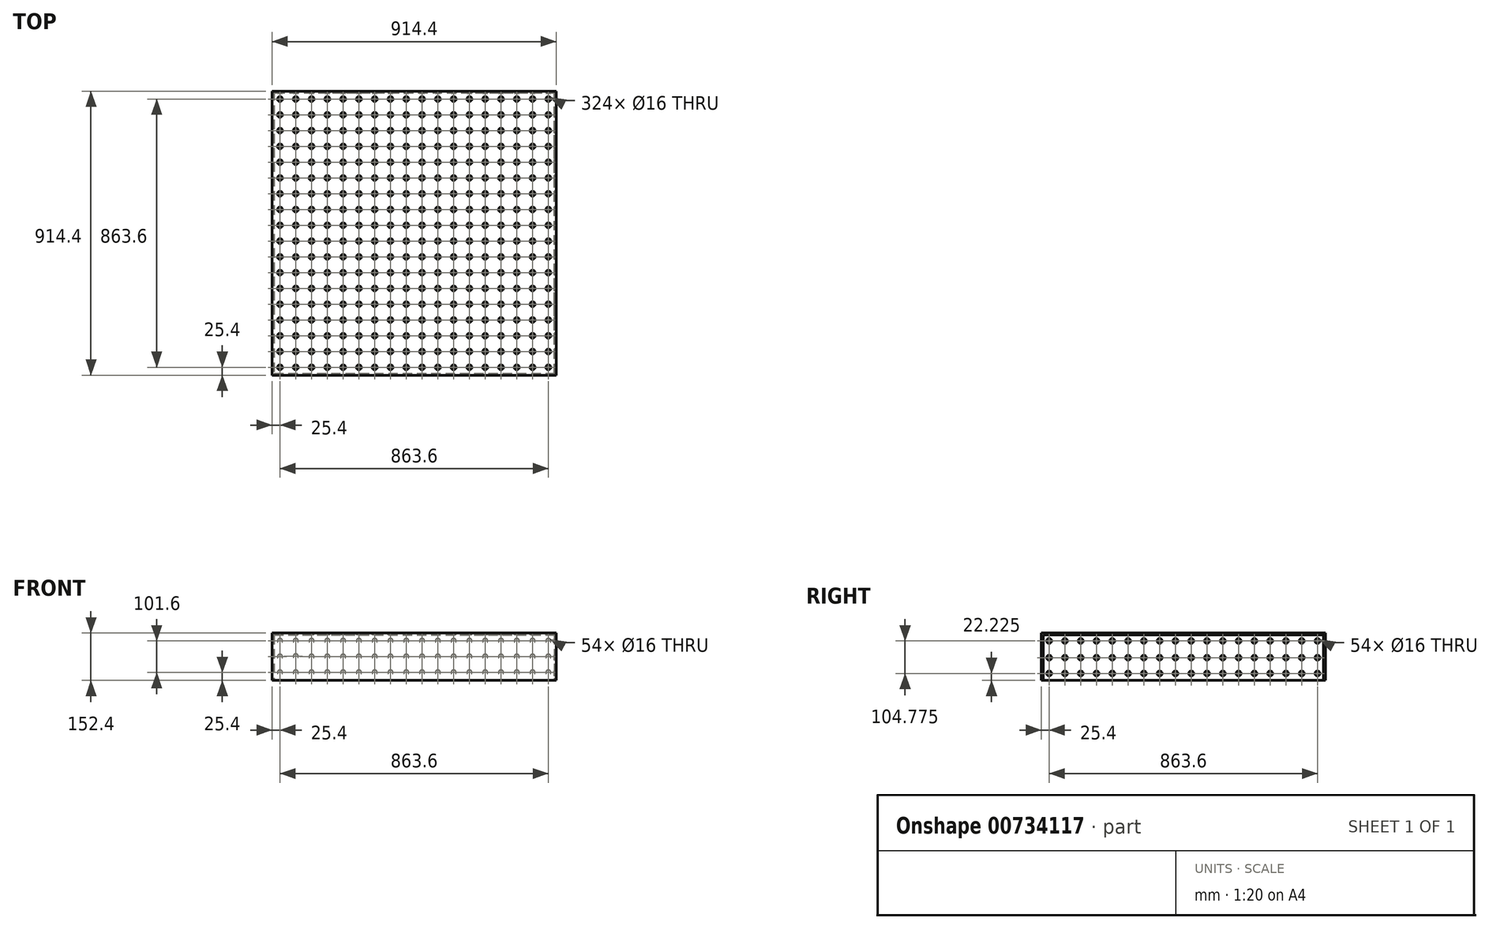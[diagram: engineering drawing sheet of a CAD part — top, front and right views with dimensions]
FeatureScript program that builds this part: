
annotation { "Feature Type Name" : "Feature", "Feature Type Description" : "" }
export const myFeature = defineFeature(function(context is Context, id is Id, definition is map)
    precondition{}
    {
        {
            var Q0;
            Q0=qCreatedBy(makeId("Top.planeOp"),FACE);
            var sketch = newSketch(context, id + "F0", { "sketchPlane" : qUnion([Q0])});
            skLineSegment(sketch, "E0.bottom", {"start": v(-457.2, 457.2) * mm, "end": v(457.2, 457.2) * mm});
            skLineSegment(sketch, "E0.top", {"start": v(-457.2, -457.2) * mm, "end": v(457.2, -457.2) * mm});
            skLineSegment(sketch, "E0.left", {"start": v(-457.2, 457.2) * mm, "end": v(-457.2, -457.2) * mm});
            skLineSegment(sketch, "E0.right", {"start": v(457.2, 457.2) * mm, "end": v(457.2, -457.2) * mm});
            skPoint(sketch, "E0.middle", {"position": v(0, 0) * mm});
            skSolve(sketch);
        }
        {
            var Q0;
            Q0 = qSketchRegion(id + "F0", true);
            extrude(context, id + "F1", {"entities" : qUnion([Q0]), "depth" : 6.35 * mm, "offsetDistance" : 25.4 * mm});
        }
        {
            var Q0;
            Q0=makeQuery(id+"F1.opExtrude","CAP_FACE",FACE,{"disambiguationData":[OSD([sQuery(id+"F0.wireOp",EDGE,"E0.bottom"),sQuery(id+"F0.wireOp",EDGE,"E0.top"),sQuery(id+"F0.wireOp",EDGE,"E0.left"),sQuery(id+"F0.wireOp",EDGE,"E0.right")])],"isStart":false});
            var sketch = newSketch(context, id + "F2", { "sketchPlane" : qUnion([Q0])});
            skLineSegment(sketch, "E1", {"start": v(-431.8, 457.2) * mm, "end": v(-431.8, -457.2) * mm, "construction": true});
            skLineSegment(sketch, "E2", {"start": v(-381, 457.2) * mm, "end": v(-381, -457.2) * mm, "construction": true});
            skLineSegment(sketch, "E3", {"start": v(-330.2, 457.2) * mm, "end": v(-330.2, -457.2) * mm, "construction": true});
            skLineSegment(sketch, "E4", {"start": v(-279.4, 457.2) * mm, "end": v(-279.4, -457.2) * mm, "construction": true});
            skLineSegment(sketch, "E5", {"start": v(-228.6, 457.2) * mm, "end": v(-228.6, -457.2) * mm, "construction": true});
            skLineSegment(sketch, "E6", {"start": v(-177.8, 457.2) * mm, "end": v(-177.8, -457.2) * mm, "construction": true});
            skLineSegment(sketch, "E7", {"start": v(-127, 457.2) * mm, "end": v(-127, -457.2) * mm, "construction": true});
            skLineSegment(sketch, "E8", {"start": v(-76.2, 457.2) * mm, "end": v(-76.2, -457.2) * mm, "construction": true});
            skLineSegment(sketch, "E9", {"start": v(-25.4, 457.2) * mm, "end": v(-25.4, -457.2) * mm, "construction": true});
            skLineSegment(sketch, "E10", {"start": v(25.4, 457.2) * mm, "end": v(25.4, -457.2) * mm, "construction": true});
            skLineSegment(sketch, "E11", {"start": v(76.2, 457.2) * mm, "end": v(76.2, -457.2) * mm, "construction": true});
            skLineSegment(sketch, "E12", {"start": v(127, 457.2) * mm, "end": v(127, -457.2) * mm, "construction": true});
            skLineSegment(sketch, "E13", {"start": v(177.8, 457.2) * mm, "end": v(177.8, -457.2) * mm, "construction": true});
            skLineSegment(sketch, "E14", {"start": v(228.6, 457.2) * mm, "end": v(228.6, -457.2) * mm, "construction": true});
            skLineSegment(sketch, "E15", {"start": v(279.4, 457.2) * mm, "end": v(279.4, -457.2) * mm, "construction": true});
            skLineSegment(sketch, "E16", {"start": v(330.2, 457.2) * mm, "end": v(330.2, -457.2) * mm, "construction": true});
            skLineSegment(sketch, "E17", {"start": v(381, 457.2) * mm, "end": v(381, -457.2) * mm, "construction": true});
            skLineSegment(sketch, "E18", {"start": v(431.8, 457.2) * mm, "end": v(431.8, -457.2) * mm, "construction": true});
            skLineSegment(sketch, "E19", {"start": v(-457.2, 431.8) * mm, "end": v(457.2, 431.8) * mm, "construction": true});
            skLineSegment(sketch, "E20", {"start": v(-457.2, 381) * mm, "end": v(457.2, 381) * mm, "construction": true});
            skLineSegment(sketch, "E21", {"start": v(-457.2, 330.2) * mm, "end": v(457.2, 330.2) * mm, "construction": true});
            skLineSegment(sketch, "E22", {"start": v(-457.2, 279.4) * mm, "end": v(457.2, 279.4) * mm, "construction": true});
            skLineSegment(sketch, "E23", {"start": v(-457.2, 228.6) * mm, "end": v(457.2, 228.6) * mm, "construction": true});
            skLineSegment(sketch, "E24", {"start": v(-457.2, 177.8) * mm, "end": v(457.2, 177.8) * mm, "construction": true});
            skLineSegment(sketch, "E25", {"start": v(-457.2, 127) * mm, "end": v(457.2, 127) * mm, "construction": true});
            skLineSegment(sketch, "E26", {"start": v(-457.2, 76.2) * mm, "end": v(457.2, 76.2) * mm, "construction": true});
            skLineSegment(sketch, "E27", {"start": v(-457.2, 25.4) * mm, "end": v(457.2, 25.4) * mm, "construction": true});
            skLineSegment(sketch, "E28", {"start": v(-457.2, -25.4) * mm, "end": v(457.2, -25.4) * mm, "construction": true});
            skLineSegment(sketch, "E29", {"start": v(-457.2, -76.2) * mm, "end": v(457.2, -76.2) * mm, "construction": true});
            skLineSegment(sketch, "E30", {"start": v(-457.2, -127) * mm, "end": v(457.2, -127) * mm, "construction": true});
            skLineSegment(sketch, "E31", {"start": v(-457.2, -177.8) * mm, "end": v(457.2, -177.8) * mm, "construction": true});
            skLineSegment(sketch, "E32", {"start": v(-457.2, -228.6) * mm, "end": v(457.2, -228.6) * mm, "construction": true});
            skLineSegment(sketch, "E33", {"start": v(-457.2, -279.4) * mm, "end": v(457.2, -279.4) * mm, "construction": true});
            skLineSegment(sketch, "E34", {"start": v(-457.2, -330.2) * mm, "end": v(457.2, -330.2) * mm, "construction": true});
            skLineSegment(sketch, "E35", {"start": v(-457.2, -381) * mm, "end": v(457.2, -381) * mm, "construction": true});
            skLineSegment(sketch, "E36", {"start": v(-457.2, -431.8) * mm, "end": v(457.2, -431.8) * mm, "construction": true});
            skCircle(sketch, "E37", {"center": v(-431.8, 431.8) * mm, "radius": 8 * mm});
            skPoint(sketch, "E38", {"position": v(-381, 431.8) * mm});
            skPoint(sketch, "E39", {"position": v(-330.2, 431.8) * mm});
            skPoint(sketch, "E40", {"position": v(-279.4, 431.8) * mm});
            skPoint(sketch, "E41", {"position": v(-228.6, 431.8) * mm});
            skPoint(sketch, "E42", {"position": v(-228.6, 381) * mm});
            skPoint(sketch, "E43", {"position": v(-279.4, 381) * mm});
            skPoint(sketch, "E44", {"position": v(-330.2, 381) * mm});
            skPoint(sketch, "E45", {"position": v(-381, 381) * mm});
            skPoint(sketch, "E46", {"position": v(-431.8, 381) * mm});
            skCircle(sketch, "E47", {"center": v(-381, 431.8) * mm, "radius": 8 * mm});
            skCircle(sketch, "E48", {"center": v(-330.2, 431.8) * mm, "radius": 8 * mm});
            skCircle(sketch, "E49", {"center": v(-279.4, 431.8) * mm, "radius": 8 * mm});
            skCircle(sketch, "E50", {"center": v(-228.6, 431.8) * mm, "radius": 6.89 * mm});
            skCircle(sketch, "E51", {"center": v(-228.6, 381) * mm, "radius": 8 * mm});
            skCircle(sketch, "E52", {"center": v(-279.4, 381) * mm, "radius": 8 * mm});
            skCircle(sketch, "E53", {"center": v(-381, 381) * mm, "radius": 8 * mm});
            skCircle(sketch, "E54", {"center": v(-431.8, 381) * mm, "radius": 8 * mm});
            skCircle(sketch, "E55", {"center": v(-431.8, 330.2) * mm, "radius": 8 * mm});
            skCircle(sketch, "E56", {"center": v(-381, 330.2) * mm, "radius": 8 * mm});
            skPoint(sketch, "E57", {"position": v(-330.2, 330.2) * mm});
            skPoint(sketch, "E58", {"position": v(-279.4, 330.2) * mm});
            skPoint(sketch, "E59", {"position": v(-228.6, 330.2) * mm});
            skPoint(sketch, "E60", {"position": v(-228.6, 279.4) * mm});
            skPoint(sketch, "E61", {"position": v(-279.4, 279.4) * mm});
            skPoint(sketch, "E62", {"position": v(-330.2, 279.4) * mm});
            skPoint(sketch, "E63", {"position": v(-381, 279.4) * mm});
            skPoint(sketch, "E64", {"position": v(-431.8, 279.4) * mm});
            skPoint(sketch, "E65", {"position": v(-431.8, 228.6) * mm});
            skPoint(sketch, "E66", {"position": v(-381, 228.6) * mm});
            skPoint(sketch, "E67", {"position": v(-330.2, 228.6) * mm});
            skPoint(sketch, "E68", {"position": v(-279.4, 228.6) * mm});
            skPoint(sketch, "E69", {"position": v(-228.6, 228.6) * mm});
            skPoint(sketch, "E70", {"position": v(-177.8, 228.6) * mm});
            skPoint(sketch, "E71", {"position": v(-177.8, 431.8) * mm});
            skPoint(sketch, "E72", {"position": v(-177.8, 381) * mm});
            skPoint(sketch, "E73", {"position": v(-177.8, 330.2) * mm});
            skPoint(sketch, "E74", {"position": v(-177.8, 279.4) * mm});
            skPoint(sketch, "E75", {"position": v(-127, 431.8) * mm});
            skPoint(sketch, "E76", {"position": v(-127, 381) * mm});
            skPoint(sketch, "E77", {"position": v(-127, 330.2) * mm});
            skPoint(sketch, "E78", {"position": v(-127, 279.4) * mm});
            skPoint(sketch, "E79", {"position": v(-127, 228.6) * mm});
            skPoint(sketch, "E80", {"position": v(-76.2, 431.8) * mm});
            skPoint(sketch, "E81", {"position": v(-76.2, 381) * mm});
            skPoint(sketch, "E82", {"position": v(-76.2, 330.2) * mm});
            skPoint(sketch, "E83", {"position": v(-76.2, 279.4) * mm});
            skPoint(sketch, "E84", {"position": v(-76.2, 228.6) * mm});
            skPoint(sketch, "E85", {"position": v(-25.4, 431.8) * mm});
            skPoint(sketch, "E86", {"position": v(-25.4, 381) * mm});
            skPoint(sketch, "E87", {"position": v(-25.4, 330.2) * mm});
            skPoint(sketch, "E88", {"position": v(-25.4, 279.4) * mm});
            skPoint(sketch, "E89", {"position": v(-25.4, 228.6) * mm});
            skPoint(sketch, "E90", {"position": v(25.4, 431.8) * mm});
            skPoint(sketch, "E91", {"position": v(25.4, 381) * mm});
            skPoint(sketch, "E92", {"position": v(25.4, 330.2) * mm});
            skPoint(sketch, "E93", {"position": v(25.4, 279.4) * mm});
            skPoint(sketch, "E94", {"position": v(25.4, 228.6) * mm});
            skPoint(sketch, "E95", {"position": v(76.2, 431.8) * mm});
            skPoint(sketch, "E96", {"position": v(76.2, 381) * mm});
            skPoint(sketch, "E97", {"position": v(76.2, 330.2) * mm});
            skPoint(sketch, "E98", {"position": v(76.2, 279.4) * mm});
            skPoint(sketch, "E99", {"position": v(76.2, 228.6) * mm});
            skPoint(sketch, "E100", {"position": v(127, 431.8) * mm});
            skPoint(sketch, "E101", {"position": v(177.8, 431.8) * mm});
            skPoint(sketch, "E102", {"position": v(228.6, 431.8) * mm});
            skPoint(sketch, "E103", {"position": v(279.4, 431.8) * mm});
            skPoint(sketch, "E104", {"position": v(330.2, 431.8) * mm});
            skPoint(sketch, "E105", {"position": v(381, 431.8) * mm});
            skPoint(sketch, "E106", {"position": v(431.8, 431.8) * mm});
            skPoint(sketch, "E107", {"position": v(127, 381) * mm});
            skPoint(sketch, "E108", {"position": v(177.8, 381) * mm});
            skPoint(sketch, "E109", {"position": v(228.6, 381) * mm});
            skPoint(sketch, "E110", {"position": v(279.4, 381) * mm});
            skPoint(sketch, "E111", {"position": v(330.2, 381) * mm});
            skPoint(sketch, "E112", {"position": v(381, 381) * mm});
            skPoint(sketch, "E113", {"position": v(431.8, 381) * mm});
            skPoint(sketch, "E114", {"position": v(127, 330.2) * mm});
            skPoint(sketch, "E115", {"position": v(177.8, 330.2) * mm});
            skPoint(sketch, "E116", {"position": v(228.6, 330.2) * mm});
            skPoint(sketch, "E117", {"position": v(279.4, 330.2) * mm});
            skPoint(sketch, "E118", {"position": v(330.2, 330.2) * mm});
            skPoint(sketch, "E119", {"position": v(381, 330.2) * mm});
            skPoint(sketch, "E120", {"position": v(431.8, 330.2) * mm});
            skPoint(sketch, "E121", {"position": v(127, 279.4) * mm});
            skPoint(sketch, "E122", {"position": v(177.8, 279.4) * mm});
            skPoint(sketch, "E123", {"position": v(228.6, 279.4) * mm});
            skPoint(sketch, "E124", {"position": v(279.4, 279.4) * mm});
            skPoint(sketch, "E125", {"position": v(330.2, 279.4) * mm});
            skPoint(sketch, "E126", {"position": v(381, 279.4) * mm});
            skPoint(sketch, "E127", {"position": v(431.8, 279.4) * mm});
            skPoint(sketch, "E128", {"position": v(127, 228.6) * mm});
            skPoint(sketch, "E129", {"position": v(177.8, 228.6) * mm});
            skPoint(sketch, "E130", {"position": v(228.6, 228.6) * mm});
            skPoint(sketch, "E131", {"position": v(279.4, 228.6) * mm});
            skPoint(sketch, "E132", {"position": v(330.2, 228.6) * mm});
            skPoint(sketch, "E133", {"position": v(381, 228.6) * mm});
            skPoint(sketch, "E134", {"position": v(431.8, 228.6) * mm});
            skPoint(sketch, "E135", {"position": v(-431.8, 177.8) * mm});
            skPoint(sketch, "E136", {"position": v(-381, 177.8) * mm});
            skPoint(sketch, "E137", {"position": v(-330.2, 177.8) * mm});
            skPoint(sketch, "E138", {"position": v(-279.4, 177.8) * mm});
            skPoint(sketch, "E139", {"position": v(-228.6, 177.8) * mm});
            skPoint(sketch, "E140", {"position": v(-177.8, 177.8) * mm});
            skPoint(sketch, "E141", {"position": v(-127, 177.8) * mm});
            skPoint(sketch, "E142", {"position": v(-76.2, 177.8) * mm});
            skPoint(sketch, "E143", {"position": v(-25.4, 177.8) * mm});
            skPoint(sketch, "E144", {"position": v(76.2, 177.8) * mm});
            skPoint(sketch, "E145", {"position": v(25.4, 177.8) * mm});
            skPoint(sketch, "E146", {"position": v(127, 177.8) * mm});
            skPoint(sketch, "E147", {"position": v(177.8, 177.8) * mm});
            skPoint(sketch, "E148", {"position": v(228.6, 177.8) * mm});
            skPoint(sketch, "E149", {"position": v(279.4, 177.8) * mm});
            skPoint(sketch, "E150", {"position": v(330.2, 177.8) * mm});
            skPoint(sketch, "E151", {"position": v(381, 177.8) * mm});
            skPoint(sketch, "E152", {"position": v(431.8, 177.8) * mm});
            skPoint(sketch, "E153", {"position": v(-431.8, 127) * mm});
            skPoint(sketch, "E154", {"position": v(-381, 127) * mm});
            skPoint(sketch, "E155", {"position": v(-330.2, 127) * mm});
            skPoint(sketch, "E156", {"position": v(-279.4, 127) * mm});
            skPoint(sketch, "E157", {"position": v(-228.6, 127) * mm});
            skPoint(sketch, "E158", {"position": v(-177.8, 127) * mm});
            skPoint(sketch, "E159", {"position": v(-127, 127) * mm});
            skPoint(sketch, "E160", {"position": v(-76.2, 127) * mm});
            skPoint(sketch, "E161", {"position": v(-25.4, 127) * mm});
            skPoint(sketch, "E162", {"position": v(25.4, 127) * mm});
            skPoint(sketch, "E163", {"position": v(76.2, 127) * mm});
            skPoint(sketch, "E164", {"position": v(127, 127) * mm});
            skPoint(sketch, "E165", {"position": v(177.8, 127) * mm});
            skPoint(sketch, "E166", {"position": v(228.6, 127) * mm});
            skPoint(sketch, "E167", {"position": v(279.4, 127) * mm});
            skPoint(sketch, "E168", {"position": v(330.2, 127) * mm});
            skPoint(sketch, "E169", {"position": v(381, 127) * mm});
            skPoint(sketch, "E170", {"position": v(431.8, 127) * mm});
            skPoint(sketch, "E171", {"position": v(431.8, 76.2) * mm});
            skPoint(sketch, "E172", {"position": v(381, 76.2) * mm});
            skPoint(sketch, "E173", {"position": v(330.2, 76.2) * mm});
            skPoint(sketch, "E174", {"position": v(279.4, 76.2) * mm});
            skPoint(sketch, "E175", {"position": v(228.6, 76.2) * mm});
            skPoint(sketch, "E176", {"position": v(177.8, 76.2) * mm});
            skPoint(sketch, "E177", {"position": v(127, 76.2) * mm});
            skPoint(sketch, "E178", {"position": v(76.2, 76.2) * mm});
            skPoint(sketch, "E179", {"position": v(25.4, 76.2) * mm});
            skPoint(sketch, "E180", {"position": v(-25.4, 76.2) * mm});
            skPoint(sketch, "E181", {"position": v(-76.2, 76.2) * mm});
            skPoint(sketch, "E182", {"position": v(-127, 76.2) * mm});
            skPoint(sketch, "E183", {"position": v(-177.8, 76.2) * mm});
            skPoint(sketch, "E184", {"position": v(-228.6, 76.2) * mm});
            skPoint(sketch, "E185", {"position": v(-279.4, 76.2) * mm});
            skPoint(sketch, "E186", {"position": v(-330.2, 76.2) * mm});
            skPoint(sketch, "E187", {"position": v(-381, 76.2) * mm});
            skPoint(sketch, "E188", {"position": v(-431.8, 76.2) * mm});
            skPoint(sketch, "E189", {"position": v(-431.8, 25.4) * mm});
            skPoint(sketch, "E190", {"position": v(-381, 25.4) * mm});
            skPoint(sketch, "E191", {"position": v(-330.2, 25.4) * mm});
            skPoint(sketch, "E192", {"position": v(-279.4, 25.4) * mm});
            skPoint(sketch, "E193", {"position": v(-228.6, 25.4) * mm});
            skPoint(sketch, "E194", {"position": v(-177.8, 25.4) * mm});
            skPoint(sketch, "E195", {"position": v(-127, 25.4) * mm});
            skPoint(sketch, "E196", {"position": v(-76.2, 25.4) * mm});
            skPoint(sketch, "E197", {"position": v(-25.4, 25.4) * mm});
            skPoint(sketch, "E198", {"position": v(25.4, 25.4) * mm});
            skPoint(sketch, "E199", {"position": v(76.2, 25.4) * mm});
            skPoint(sketch, "E200", {"position": v(127, 25.4) * mm});
            skPoint(sketch, "E201", {"position": v(177.8, 25.4) * mm});
            skPoint(sketch, "E202", {"position": v(228.6, 25.4) * mm});
            skPoint(sketch, "E203", {"position": v(279.4, 25.4) * mm});
            skPoint(sketch, "E204", {"position": v(330.2, 25.4) * mm});
            skPoint(sketch, "E205", {"position": v(381, 25.4) * mm});
            skPoint(sketch, "E206", {"position": v(431.8, 25.4) * mm});
            skPoint(sketch, "E207", {"position": v(431.8, -25.4) * mm});
            skPoint(sketch, "E208", {"position": v(381, -25.4) * mm});
            skPoint(sketch, "E209", {"position": v(330.2, -25.4) * mm});
            skPoint(sketch, "E210", {"position": v(279.4, -25.4) * mm});
            skPoint(sketch, "E211", {"position": v(228.6, -25.4) * mm});
            skPoint(sketch, "E212", {"position": v(177.8, -25.4) * mm});
            skPoint(sketch, "E213", {"position": v(127, -25.4) * mm});
            skPoint(sketch, "E214", {"position": v(76.2, -25.4) * mm});
            skPoint(sketch, "E215", {"position": v(25.4, -25.4) * mm});
            skPoint(sketch, "E216", {"position": v(-25.4, -25.4) * mm});
            skPoint(sketch, "E217", {"position": v(-76.2, -25.4) * mm});
            skPoint(sketch, "E218", {"position": v(-127, -25.4) * mm});
            skPoint(sketch, "E219", {"position": v(-177.8, -25.4) * mm});
            skPoint(sketch, "E220", {"position": v(-228.6, -25.4) * mm});
            skPoint(sketch, "E221", {"position": v(-279.4, -25.4) * mm});
            skPoint(sketch, "E222", {"position": v(-330.2, -25.4) * mm});
            skPoint(sketch, "E223", {"position": v(-381, -25.4) * mm});
            skPoint(sketch, "E224", {"position": v(-431.8, -25.4) * mm});
            skPoint(sketch, "E225", {"position": v(-431.8, -76.2) * mm});
            skPoint(sketch, "E226", {"position": v(-381, -76.2) * mm});
            skPoint(sketch, "E227", {"position": v(-330.2, -76.2) * mm});
            skPoint(sketch, "E228", {"position": v(-279.4, -76.2) * mm});
            skPoint(sketch, "E229", {"position": v(-228.6, -76.2) * mm});
            skPoint(sketch, "E230", {"position": v(-177.8, -76.2) * mm});
            skPoint(sketch, "E231", {"position": v(-127, -76.2) * mm});
            skPoint(sketch, "E232", {"position": v(-76.2, -76.2) * mm});
            skPoint(sketch, "E233", {"position": v(-25.4, -76.2) * mm});
            skPoint(sketch, "E234", {"position": v(25.4, -76.2) * mm});
            skPoint(sketch, "E235", {"position": v(76.2, -76.2) * mm});
            skPoint(sketch, "E236", {"position": v(127, -76.2) * mm});
            skPoint(sketch, "E237", {"position": v(177.8, -76.2) * mm});
            skPoint(sketch, "E238", {"position": v(228.6, -76.2) * mm});
            skPoint(sketch, "E239", {"position": v(279.4, -76.2) * mm});
            skPoint(sketch, "E240", {"position": v(330.2, -76.2) * mm});
            skPoint(sketch, "E241", {"position": v(381, -76.2) * mm});
            skPoint(sketch, "E242", {"position": v(431.8, -76.2) * mm});
            skPoint(sketch, "E243", {"position": v(431.8, -127) * mm});
            skPoint(sketch, "E244", {"position": v(381, -127) * mm});
            skPoint(sketch, "E245", {"position": v(330.2, -127) * mm});
            skPoint(sketch, "E246", {"position": v(279.4, -127) * mm});
            skPoint(sketch, "E247", {"position": v(228.6, -127) * mm});
            skPoint(sketch, "E248", {"position": v(177.8, -127) * mm});
            skPoint(sketch, "E249", {"position": v(127, -127) * mm});
            skPoint(sketch, "E250", {"position": v(76.2, -127) * mm});
            skPoint(sketch, "E251", {"position": v(25.4, -127) * mm});
            skPoint(sketch, "E252", {"position": v(-25.4, -127) * mm});
            skPoint(sketch, "E253", {"position": v(-76.2, -127) * mm});
            skPoint(sketch, "E254", {"position": v(-127, -127) * mm});
            skPoint(sketch, "E255", {"position": v(-177.8, -127) * mm});
            skPoint(sketch, "E256", {"position": v(-228.6, -127) * mm});
            skPoint(sketch, "E257", {"position": v(-279.4, -127) * mm});
            skPoint(sketch, "E258", {"position": v(-330.2, -127) * mm});
            skPoint(sketch, "E259", {"position": v(-381, -127) * mm});
            skPoint(sketch, "E260", {"position": v(-431.8, -127) * mm});
            skPoint(sketch, "E261", {"position": v(-431.8, -177.8) * mm});
            skPoint(sketch, "E262", {"position": v(-381, -177.8) * mm});
            skPoint(sketch, "E263", {"position": v(-330.2, -177.8) * mm});
            skPoint(sketch, "E264", {"position": v(-279.4, -177.8) * mm});
            skPoint(sketch, "E265", {"position": v(-228.6, -177.8) * mm});
            skPoint(sketch, "E266", {"position": v(-177.8, -177.8) * mm});
            skPoint(sketch, "E267", {"position": v(-127, -177.8) * mm});
            skPoint(sketch, "E268", {"position": v(-76.2, -177.8) * mm});
            skPoint(sketch, "E269", {"position": v(-25.4, -177.8) * mm});
            skPoint(sketch, "E270", {"position": v(25.4, -177.8) * mm});
            skPoint(sketch, "E271", {"position": v(76.2, -177.8) * mm});
            skPoint(sketch, "E272", {"position": v(127, -177.8) * mm});
            skPoint(sketch, "E273", {"position": v(177.8, -177.8) * mm});
            skPoint(sketch, "E274", {"position": v(228.6, -177.8) * mm});
            skPoint(sketch, "E275", {"position": v(279.4, -177.8) * mm});
            skPoint(sketch, "E276", {"position": v(330.2, -177.8) * mm});
            skPoint(sketch, "E277", {"position": v(381, -177.8) * mm});
            skPoint(sketch, "E278", {"position": v(431.8, -177.8) * mm});
            skPoint(sketch, "E279", {"position": v(431.8, -228.6) * mm});
            skPoint(sketch, "E280", {"position": v(381, -228.6) * mm});
            skPoint(sketch, "E281", {"position": v(330.2, -228.6) * mm});
            skPoint(sketch, "E282", {"position": v(279.4, -228.6) * mm});
            skPoint(sketch, "E283", {"position": v(228.6, -228.6) * mm});
            skPoint(sketch, "E284", {"position": v(177.8, -228.6) * mm});
            skPoint(sketch, "E285", {"position": v(127, -228.6) * mm});
            skPoint(sketch, "E286", {"position": v(76.2, -228.6) * mm});
            skPoint(sketch, "E287", {"position": v(25.4, -228.6) * mm});
            skPoint(sketch, "E288", {"position": v(-25.4, -228.6) * mm});
            skPoint(sketch, "E289", {"position": v(-76.2, -228.6) * mm});
            skPoint(sketch, "E290", {"position": v(-127, -228.6) * mm});
            skPoint(sketch, "E291", {"position": v(-177.8, -228.6) * mm});
            skPoint(sketch, "E292", {"position": v(-228.6, -228.6) * mm});
            skPoint(sketch, "E293", {"position": v(-279.4, -228.6) * mm});
            skPoint(sketch, "E294", {"position": v(-330.2, -228.6) * mm});
            skPoint(sketch, "E295", {"position": v(-381, -228.6) * mm});
            skPoint(sketch, "E296", {"position": v(-431.8, -228.6) * mm});
            skPoint(sketch, "E297", {"position": v(-431.8, -279.4) * mm});
            skPoint(sketch, "E298", {"position": v(-381, -279.4) * mm});
            skPoint(sketch, "E299", {"position": v(-330.2, -279.4) * mm});
            skPoint(sketch, "E300", {"position": v(-279.4, -279.4) * mm});
            skPoint(sketch, "E301", {"position": v(-228.6, -279.4) * mm});
            skPoint(sketch, "E302", {"position": v(-177.8, -279.4) * mm});
            skPoint(sketch, "E303", {"position": v(-127, -279.4) * mm});
            skPoint(sketch, "E304", {"position": v(-76.2, -279.4) * mm});
            skPoint(sketch, "E305", {"position": v(-25.4, -279.4) * mm});
            skPoint(sketch, "E306", {"position": v(25.4, -279.4) * mm});
            skPoint(sketch, "E307", {"position": v(76.2, -279.4) * mm});
            skPoint(sketch, "E308", {"position": v(127, -279.4) * mm});
            skPoint(sketch, "E309", {"position": v(177.8, -279.4) * mm});
            skPoint(sketch, "E310", {"position": v(228.6, -279.4) * mm});
            skPoint(sketch, "E311", {"position": v(279.4, -279.4) * mm});
            skPoint(sketch, "E312", {"position": v(330.2, -279.4) * mm});
            skPoint(sketch, "E313", {"position": v(381, -279.4) * mm});
            skPoint(sketch, "E314", {"position": v(431.8, -279.4) * mm});
            skPoint(sketch, "E315", {"position": v(431.8, -330.2) * mm});
            skPoint(sketch, "E316", {"position": v(381, -330.2) * mm});
            skPoint(sketch, "E317", {"position": v(330.2, -330.2) * mm});
            skPoint(sketch, "E318", {"position": v(279.4, -330.2) * mm});
            skPoint(sketch, "E319", {"position": v(228.6, -330.2) * mm});
            skPoint(sketch, "E320", {"position": v(177.8, -330.2) * mm});
            skPoint(sketch, "E321", {"position": v(127, -330.2) * mm});
            skPoint(sketch, "E322", {"position": v(76.2, -330.2) * mm});
            skPoint(sketch, "E323", {"position": v(25.4, -330.2) * mm});
            skPoint(sketch, "E324", {"position": v(-25.4, -330.2) * mm});
            skPoint(sketch, "E325", {"position": v(-76.2, -330.2) * mm});
            skPoint(sketch, "E326", {"position": v(-127, -330.2) * mm});
            skPoint(sketch, "E327", {"position": v(-177.8, -330.2) * mm});
            skPoint(sketch, "E328", {"position": v(-228.6, -330.2) * mm});
            skPoint(sketch, "E329", {"position": v(-279.4, -330.2) * mm});
            skPoint(sketch, "E330", {"position": v(-330.2, -330.2) * mm});
            skPoint(sketch, "E331", {"position": v(-381, -330.2) * mm});
            skPoint(sketch, "E332", {"position": v(-431.8, -330.2) * mm});
            skPoint(sketch, "E333", {"position": v(-431.8, -381) * mm});
            skPoint(sketch, "E334", {"position": v(-381, -381) * mm});
            skPoint(sketch, "E335", {"position": v(-330.2, -381) * mm});
            skPoint(sketch, "E336", {"position": v(-279.4, -381) * mm});
            skPoint(sketch, "E337", {"position": v(-228.6, -381) * mm});
            skPoint(sketch, "E338", {"position": v(-177.8, -381) * mm});
            skPoint(sketch, "E339", {"position": v(-127, -381) * mm});
            skPoint(sketch, "E340", {"position": v(-76.2, -381) * mm});
            skPoint(sketch, "E341", {"position": v(-25.4, -381) * mm});
            skPoint(sketch, "E342", {"position": v(25.4, -381) * mm});
            skPoint(sketch, "E343", {"position": v(76.2, -381) * mm});
            skPoint(sketch, "E344", {"position": v(127, -381) * mm});
            skPoint(sketch, "E345", {"position": v(177.8, -381) * mm});
            skPoint(sketch, "E346", {"position": v(228.6, -381) * mm});
            skPoint(sketch, "E347", {"position": v(279.4, -381) * mm});
            skPoint(sketch, "E348", {"position": v(330.2, -381) * mm});
            skPoint(sketch, "E349", {"position": v(381, -381) * mm});
            skPoint(sketch, "E350", {"position": v(431.8, -381) * mm});
            skPoint(sketch, "E351", {"position": v(431.8, -431.8) * mm});
            skPoint(sketch, "E352", {"position": v(381, -431.8) * mm});
            skPoint(sketch, "E353", {"position": v(330.2, -431.8) * mm});
            skPoint(sketch, "E354", {"position": v(279.4, -431.8) * mm});
            skPoint(sketch, "E355", {"position": v(228.6, -431.8) * mm});
            skPoint(sketch, "E356", {"position": v(177.8, -431.8) * mm});
            skPoint(sketch, "E357", {"position": v(127, -431.8) * mm});
            skPoint(sketch, "E358", {"position": v(76.2, -431.8) * mm});
            skPoint(sketch, "E359", {"position": v(-431.8, -431.8) * mm});
            skPoint(sketch, "E360", {"position": v(-381, -431.8) * mm});
            skPoint(sketch, "E361", {"position": v(-330.2, -431.8) * mm});
            skPoint(sketch, "E362", {"position": v(-279.4, -431.8) * mm});
            skPoint(sketch, "E363", {"position": v(-228.6, -431.8) * mm});
            skPoint(sketch, "E364", {"position": v(-177.8, -431.8) * mm});
            skPoint(sketch, "E365", {"position": v(-127, -431.8) * mm});
            skPoint(sketch, "E366", {"position": v(-76.2, -431.8) * mm});
            skPoint(sketch, "E367", {"position": v(-25.4, -431.8) * mm});
            skPoint(sketch, "E368", {"position": v(25.4, -431.8) * mm});
            skCircle(sketch, "E369", {"center": v(-177.8, 431.8) * mm, "radius": 8.14 * mm});
            skCircle(sketch, "E370", {"center": v(-127, 431.8) * mm, "radius": 8 * mm});
            skCircle(sketch, "E371", {"center": v(-76.2, 431.8) * mm, "radius": 8 * mm});
            skCircle(sketch, "E372", {"center": v(-25.4, 431.8) * mm, "radius": 8 * mm});
            skCircle(sketch, "E373", {"center": v(-25.4, 381) * mm, "radius": 8 * mm});
            skCircle(sketch, "E374", {"center": v(-76.2, 381) * mm, "radius": 8 * mm});
            skCircle(sketch, "E375", {"center": v(-127, 381) * mm, "radius": 8 * mm});
            skCircle(sketch, "E376", {"center": v(-330.2, 381) * mm, "radius": 7.81 * mm});
            skCircle(sketch, "E377", {"center": v(-279.4, 330.2) * mm, "radius": 8 * mm});
            skCircle(sketch, "E378", {"center": v(-228.6, 330.2) * mm, "radius": 8 * mm});
            skCircle(sketch, "E379", {"center": v(-177.8, 330.2) * mm, "radius": 8 * mm});
            skCircle(sketch, "E380", {"center": v(-127, 330.2) * mm, "radius": 8 * mm});
            skCircle(sketch, "E381", {"center": v(-76.2, 330.2) * mm, "radius": 8 * mm});
            skCircle(sketch, "E382", {"center": v(-25.4, 330.2) * mm, "radius": 8 * mm});
            skCircle(sketch, "E383", {"center": v(-25.4, 279.4) * mm, "radius": 8 * mm});
            skCircle(sketch, "E384", {"center": v(-76.2, 279.4) * mm, "radius": 8 * mm});
            skCircle(sketch, "E385", {"center": v(-127, 279.4) * mm, "radius": 8 * mm});
            skCircle(sketch, "E386", {"center": v(-177.8, 279.4) * mm, "radius": 8 * mm});
            skCircle(sketch, "E387", {"center": v(-228.6, 279.4) * mm, "radius": 7.98 * mm});
            skCircle(sketch, "E388", {"center": v(-279.4, 279.4) * mm, "radius": 8.29 * mm});
            skCircle(sketch, "E389", {"center": v(-330.2, 279.4) * mm, "radius": 8 * mm});
            skCircle(sketch, "E390", {"center": v(-381, 279.4) * mm, "radius": 8 * mm});
            skCircle(sketch, "E391", {"center": v(-431.8, 279.4) * mm, "radius": 8 * mm});
            skCircle(sketch, "E392", {"center": v(25.4, 431.8) * mm, "radius": 8 * mm});
            skCircle(sketch, "E393", {"center": v(76.2, 431.8) * mm, "radius": 8 * mm});
            skCircle(sketch, "E394", {"center": v(127, 431.8) * mm, "radius": 8 * mm});
            skCircle(sketch, "E395", {"center": v(-177.8, 381) * mm, "radius": 8 * mm});
            skCircle(sketch, "E396", {"center": v(-330.2, 330.2) * mm, "radius": 8 * mm});
            skCircle(sketch, "E397", {"center": v(25.4, 381) * mm, "radius": 8 * mm});
            skCircle(sketch, "E398", {"center": v(76.2, 381) * mm, "radius": 8 * mm});
            skCircle(sketch, "E399", {"center": v(127, 381) * mm, "radius": 8 * mm});
            skCircle(sketch, "E400", {"center": v(25.4, 330.2) * mm, "radius": 8 * mm});
            skCircle(sketch, "E401", {"center": v(76.2, 330.2) * mm, "radius": 8 * mm});
            skCircle(sketch, "E402", {"center": v(127, 330.2) * mm, "radius": 8 * mm});
            skCircle(sketch, "E403", {"center": v(25.4, 279.4) * mm, "radius": 8 * mm});
            skCircle(sketch, "E404", {"center": v(76.2, 279.4) * mm, "radius": 8 * mm});
            skCircle(sketch, "E405", {"center": v(127, 279.4) * mm, "radius": 8 * mm});
            skCircle(sketch, "E406", {"center": v(177.8, 431.8) * mm, "radius": 8 * mm});
            skCircle(sketch, "E407", {"center": v(177.8, 381) * mm, "radius": 8 * mm});
            skCircle(sketch, "E408", {"center": v(177.8, 330.2) * mm, "radius": 8 * mm});
            skCircle(sketch, "E409", {"center": v(177.8, 279.4) * mm, "radius": 8 * mm});
            skCircle(sketch, "E410", {"center": v(228.6, 431.8) * mm, "radius": 8 * mm});
            skCircle(sketch, "E411", {"center": v(228.6, 381) * mm, "radius": 8 * mm});
            skCircle(sketch, "E412", {"center": v(228.6, 330.2) * mm, "radius": 8 * mm});
            skCircle(sketch, "E413", {"center": v(279.4, 431.8) * mm, "radius": 8 * mm});
            skCircle(sketch, "E414", {"center": v(279.4, 381) * mm, "radius": 8 * mm});
            skCircle(sketch, "E415", {"center": v(279.4, 330.2) * mm, "radius": 8 * mm});
            skCircle(sketch, "E416", {"center": v(228.6, 279.4) * mm, "radius": 8 * mm});
            skCircle(sketch, "E417", {"center": v(279.4, 279.4) * mm, "radius": 8 * mm});
            skCircle(sketch, "E418", {"center": v(330.2, 431.8) * mm, "radius": 8 * mm});
            skCircle(sketch, "E419", {"center": v(330.2, 381) * mm, "radius": 8 * mm});
            skCircle(sketch, "E420", {"center": v(330.2, 330.2) * mm, "radius": 8 * mm});
            skCircle(sketch, "E421", {"center": v(330.2, 279.4) * mm, "radius": 8 * mm});
            skCircle(sketch, "E422", {"center": v(381, 431.8) * mm, "radius": 8 * mm});
            skCircle(sketch, "E423", {"center": v(381, 381) * mm, "radius": 8 * mm});
            skCircle(sketch, "E424", {"center": v(381, 330.2) * mm, "radius": 8 * mm});
            skCircle(sketch, "E425", {"center": v(381, 279.4) * mm, "radius": 8 * mm});
            skCircle(sketch, "E426", {"center": v(431.8, 279.4) * mm, "radius": 8 * mm});
            skCircle(sketch, "E427", {"center": v(431.8, 330.2) * mm, "radius": 8 * mm});
            skCircle(sketch, "E428", {"center": v(431.8, 381) * mm, "radius": 8 * mm});
            skCircle(sketch, "E429", {"center": v(431.8, 431.8) * mm, "radius": 8 * mm});
            skCircle(sketch, "E430", {"center": v(-431.8, 228.6) * mm, "radius": 8 * mm});
            skCircle(sketch, "E431", {"center": v(-381, 228.6) * mm, "radius": 8 * mm});
            skCircle(sketch, "E432", {"center": v(-330.2, 228.6) * mm, "radius": 8 * mm});
            skCircle(sketch, "E433", {"center": v(-279.4, 228.6) * mm, "radius": 8 * mm});
            skCircle(sketch, "E434", {"center": v(-228.6, 228.6) * mm, "radius": 8 * mm});
            skCircle(sketch, "E435", {"center": v(-177.8, 228.6) * mm, "radius": 8 * mm});
            skCircle(sketch, "E436", {"center": v(-127, 228.6) * mm, "radius": 8 * mm});
            skCircle(sketch, "E437", {"center": v(-76.2, 228.6) * mm, "radius": 8 * mm});
            skCircle(sketch, "E438", {"center": v(-25.4, 228.6) * mm, "radius": 8 * mm});
            skCircle(sketch, "E439", {"center": v(25.4, 228.6) * mm, "radius": 8 * mm});
            skCircle(sketch, "E440", {"center": v(76.2, 228.6) * mm, "radius": 8 * mm});
            skCircle(sketch, "E441", {"center": v(127, 228.6) * mm, "radius": 8 * mm});
            skCircle(sketch, "E442", {"center": v(177.8, 228.6) * mm, "radius": 8 * mm});
            skCircle(sketch, "E443", {"center": v(228.6, 228.6) * mm, "radius": 8 * mm});
            skCircle(sketch, "E444", {"center": v(279.4, 228.6) * mm, "radius": 8 * mm});
            skCircle(sketch, "E445", {"center": v(330.2, 228.6) * mm, "radius": 8 * mm});
            skCircle(sketch, "E446", {"center": v(381, 228.6) * mm, "radius": 8 * mm});
            skCircle(sketch, "E447", {"center": v(431.8, 228.6) * mm, "radius": 8 * mm});
            skCircle(sketch, "E448", {"center": v(431.8, 177.8) * mm, "radius": 8 * mm});
            skCircle(sketch, "E449", {"center": v(381, 177.8) * mm, "radius": 8 * mm});
            skCircle(sketch, "E450", {"center": v(330.2, 177.8) * mm, "radius": 8 * mm});
            skCircle(sketch, "E451", {"center": v(279.4, 177.8) * mm, "radius": 8 * mm});
            skCircle(sketch, "E452", {"center": v(228.6, 177.8) * mm, "radius": 8 * mm});
            skCircle(sketch, "E453", {"center": v(177.8, 177.8) * mm, "radius": 8 * mm});
            skCircle(sketch, "E454", {"center": v(127, 177.8) * mm, "radius": 8 * mm});
            skCircle(sketch, "E455", {"center": v(76.2, 177.8) * mm, "radius": 8 * mm});
            skCircle(sketch, "E456", {"center": v(25.4, 177.8) * mm, "radius": 8 * mm});
            skCircle(sketch, "E457", {"center": v(-25.4, 177.8) * mm, "radius": 8 * mm});
            skCircle(sketch, "E458", {"center": v(-76.2, 177.8) * mm, "radius": 8 * mm});
            skCircle(sketch, "E459", {"center": v(-127, 177.8) * mm, "radius": 8 * mm});
            skCircle(sketch, "E460", {"center": v(-177.8, 177.8) * mm, "radius": 8 * mm});
            skCircle(sketch, "E461", {"center": v(-228.6, 177.8) * mm, "radius": 8 * mm});
            skCircle(sketch, "E462", {"center": v(-279.4, 177.8) * mm, "radius": 8 * mm});
            skCircle(sketch, "E463", {"center": v(-330.2, 177.8) * mm, "radius": 8 * mm});
            skCircle(sketch, "E464", {"center": v(-381, 177.8) * mm, "radius": 8 * mm});
            skCircle(sketch, "E465", {"center": v(-431.8, 177.8) * mm, "radius": 8 * mm});
            skCircle(sketch, "E466", {"center": v(-431.8, 127) * mm, "radius": 8 * mm});
            skCircle(sketch, "E467", {"center": v(-381, 127) * mm, "radius": 8 * mm});
            skCircle(sketch, "E468", {"center": v(-330.2, 127) * mm, "radius": 8 * mm});
            skCircle(sketch, "E469", {"center": v(-279.4, 127) * mm, "radius": 8 * mm});
            skCircle(sketch, "E470", {"center": v(-228.6, 127) * mm, "radius": 8 * mm});
            skCircle(sketch, "E471", {"center": v(-177.8, 127) * mm, "radius": 8 * mm});
            skCircle(sketch, "E472", {"center": v(-127, 127) * mm, "radius": 8 * mm});
            skCircle(sketch, "E473", {"center": v(-76.2, 127) * mm, "radius": 8 * mm});
            skCircle(sketch, "E474", {"center": v(-25.4, 127) * mm, "radius": 8 * mm});
            skCircle(sketch, "E475", {"center": v(25.4, 127) * mm, "radius": 8 * mm});
            skCircle(sketch, "E476", {"center": v(76.2, 127) * mm, "radius": 8 * mm});
            skCircle(sketch, "E477", {"center": v(127, 127) * mm, "radius": 8 * mm});
            skCircle(sketch, "E478", {"center": v(177.8, 127) * mm, "radius": 8 * mm});
            skCircle(sketch, "E479", {"center": v(228.6, 127) * mm, "radius": 8 * mm});
            skCircle(sketch, "E480", {"center": v(279.4, 127) * mm, "radius": 8 * mm});
            skCircle(sketch, "E481", {"center": v(330.2, 127) * mm, "radius": 8 * mm});
            skCircle(sketch, "E482", {"center": v(381, 127) * mm, "radius": 8 * mm});
            skCircle(sketch, "E483", {"center": v(431.8, 127) * mm, "radius": 8 * mm});
            skCircle(sketch, "E484", {"center": v(431.8, 76.2) * mm, "radius": 8 * mm});
            skCircle(sketch, "E485", {"center": v(381, 76.2) * mm, "radius": 8 * mm});
            skCircle(sketch, "E486", {"center": v(330.2, 76.2) * mm, "radius": 8 * mm});
            skCircle(sketch, "E487", {"center": v(279.4, 76.2) * mm, "radius": 8 * mm});
            skCircle(sketch, "E488", {"center": v(228.6, 76.2) * mm, "radius": 8 * mm});
            skCircle(sketch, "E489", {"center": v(177.8, 76.2) * mm, "radius": 8 * mm});
            skCircle(sketch, "E490", {"center": v(127, 76.2) * mm, "radius": 8 * mm});
            skCircle(sketch, "E491", {"center": v(76.2, 76.2) * mm, "radius": 8 * mm});
            skCircle(sketch, "E492", {"center": v(25.4, 76.2) * mm, "radius": 8 * mm});
            skCircle(sketch, "E493", {"center": v(-25.4, 76.2) * mm, "radius": 8 * mm});
            skCircle(sketch, "E494", {"center": v(-76.2, 76.2) * mm, "radius": 8 * mm});
            skCircle(sketch, "E495", {"center": v(-127, 76.2) * mm, "radius": 8 * mm});
            skCircle(sketch, "E496", {"center": v(-177.8, 76.2) * mm, "radius": 8 * mm});
            skCircle(sketch, "E497", {"center": v(-228.6, 76.2) * mm, "radius": 8 * mm});
            skCircle(sketch, "E498", {"center": v(-279.4, 76.2) * mm, "radius": 8 * mm});
            skCircle(sketch, "E499", {"center": v(-330.2, 76.2) * mm, "radius": 8 * mm});
            skCircle(sketch, "E500", {"center": v(-381, 76.2) * mm, "radius": 8 * mm});
            skCircle(sketch, "E501", {"center": v(-431.8, 76.2) * mm, "radius": 8 * mm});
            skCircle(sketch, "E502", {"center": v(-431.8, 25.4) * mm, "radius": 8 * mm});
            skCircle(sketch, "E503", {"center": v(-381, 25.4) * mm, "radius": 8 * mm});
            skCircle(sketch, "E504", {"center": v(-330.2, 25.4) * mm, "radius": 8 * mm});
            skCircle(sketch, "E505", {"center": v(-279.4, 25.4) * mm, "radius": 8 * mm});
            skCircle(sketch, "E506", {"center": v(-228.6, 25.4) * mm, "radius": 8 * mm});
            skCircle(sketch, "E507", {"center": v(-177.8, 25.4) * mm, "radius": 8 * mm});
            skCircle(sketch, "E508", {"center": v(-127, 25.4) * mm, "radius": 8 * mm});
            skCircle(sketch, "E509", {"center": v(-76.2, 25.4) * mm, "radius": 8 * mm});
            skCircle(sketch, "E510", {"center": v(-25.4, 25.4) * mm, "radius": 8 * mm});
            skCircle(sketch, "E511", {"center": v(25.4, 25.4) * mm, "radius": 8 * mm});
            skCircle(sketch, "E512", {"center": v(76.2, 25.4) * mm, "radius": 8 * mm});
            skCircle(sketch, "E513", {"center": v(127, 25.4) * mm, "radius": 8 * mm});
            skCircle(sketch, "E514", {"center": v(177.8, 25.4) * mm, "radius": 8 * mm});
            skCircle(sketch, "E515", {"center": v(228.6, 25.4) * mm, "radius": 8 * mm});
            skCircle(sketch, "E516", {"center": v(279.4, 25.4) * mm, "radius": 8 * mm});
            skCircle(sketch, "E517", {"center": v(330.2, 25.4) * mm, "radius": 8 * mm});
            skCircle(sketch, "E518", {"center": v(381, 25.4) * mm, "radius": 8 * mm});
            skCircle(sketch, "E519", {"center": v(431.8, 25.4) * mm, "radius": 8 * mm});
            skCircle(sketch, "E520", {"center": v(-228.6, -25.4) * mm, "radius": 8 * mm});
            skCircle(sketch, "E521", {"center": v(-177.8, -25.4) * mm, "radius": 8 * mm});
            skCircle(sketch, "E522", {"center": v(-127, -25.4) * mm, "radius": 8 * mm});
            skCircle(sketch, "E523", {"center": v(-76.2, -25.4) * mm, "radius": 8 * mm});
            skCircle(sketch, "E524", {"center": v(-25.4, -25.4) * mm, "radius": 8 * mm});
            skCircle(sketch, "E525", {"center": v(25.4, -25.4) * mm, "radius": 8 * mm});
            skCircle(sketch, "E526", {"center": v(76.2, -25.4) * mm, "radius": 8 * mm});
            skCircle(sketch, "E527", {"center": v(127, -25.4) * mm, "radius": 8 * mm});
            skCircle(sketch, "E528", {"center": v(177.8, -25.4) * mm, "radius": 8 * mm});
            skCircle(sketch, "E529", {"center": v(228.6, -25.4) * mm, "radius": 8 * mm});
            skCircle(sketch, "E530", {"center": v(279.4, -25.4) * mm, "radius": 8 * mm});
            skCircle(sketch, "E531", {"center": v(330.2, -25.4) * mm, "radius": 8 * mm});
            skCircle(sketch, "E532", {"center": v(381, -25.4) * mm, "radius": 8 * mm});
            skCircle(sketch, "E533", {"center": v(431.8, -25.4) * mm, "radius": 8 * mm});
            skCircle(sketch, "E534", {"center": v(431.8, -76.2) * mm, "radius": 8 * mm});
            skCircle(sketch, "E535", {"center": v(381, -76.2) * mm, "radius": 8 * mm});
            skCircle(sketch, "E536", {"center": v(279.4, -76.2) * mm, "radius": 8 * mm});
            skCircle(sketch, "E537", {"center": v(330.2, -76.2) * mm, "radius": 8 * mm});
            skCircle(sketch, "E538", {"center": v(228.6, -76.2) * mm, "radius": 8 * mm});
            skCircle(sketch, "E539", {"center": v(177.8, -76.2) * mm, "radius": 8 * mm});
            skCircle(sketch, "E540", {"center": v(127, -76.2) * mm, "radius": 8 * mm});
            skCircle(sketch, "E541", {"center": v(76.2, -76.2) * mm, "radius": 8 * mm});
            skCircle(sketch, "E542", {"center": v(25.4, -76.2) * mm, "radius": 8 * mm});
            skCircle(sketch, "E543", {"center": v(-25.4, -76.2) * mm, "radius": 8 * mm});
            skCircle(sketch, "E544", {"center": v(-76.2, -76.2) * mm, "radius": 8 * mm});
            skCircle(sketch, "E545", {"center": v(-127, -76.2) * mm, "radius": 8 * mm});
            skCircle(sketch, "E546", {"center": v(-177.8, -76.2) * mm, "radius": 8 * mm});
            skCircle(sketch, "E547", {"center": v(-228.6, -76.2) * mm, "radius": 8 * mm});
            skCircle(sketch, "E548", {"center": v(-431.8, -25.4) * mm, "radius": 8 * mm});
            skCircle(sketch, "E549", {"center": v(-381, -25.4) * mm, "radius": 8 * mm});
            skCircle(sketch, "E550", {"center": v(-330.2, -25.4) * mm, "radius": 8 * mm});
            skCircle(sketch, "E551", {"center": v(-279.4, -25.4) * mm, "radius": 8 * mm});
            skCircle(sketch, "E552", {"center": v(-279.4, -76.2) * mm, "radius": 8 * mm});
            skCircle(sketch, "E553", {"center": v(-330.2, -76.2) * mm, "radius": 8 * mm});
            skCircle(sketch, "E554", {"center": v(-381, -76.2) * mm, "radius": 8 * mm});
            skCircle(sketch, "E555", {"center": v(-431.8, -76.2) * mm, "radius": 8 * mm});
            skCircle(sketch, "E556", {"center": v(-431.8, -127) * mm, "radius": 8 * mm});
            skCircle(sketch, "E557", {"center": v(-381, -127) * mm, "radius": 8 * mm});
            skCircle(sketch, "E558", {"center": v(-330.2, -127) * mm, "radius": 8 * mm});
            skCircle(sketch, "E559", {"center": v(-279.4, -127) * mm, "radius": 8 * mm});
            skCircle(sketch, "E560", {"center": v(-228.6, -127) * mm, "radius": 8 * mm});
            skCircle(sketch, "E561", {"center": v(-177.8, -127) * mm, "radius": 8 * mm});
            skCircle(sketch, "E562", {"center": v(-127, -127) * mm, "radius": 8 * mm});
            skCircle(sketch, "E563", {"center": v(-76.2, -127) * mm, "radius": 8 * mm});
            skCircle(sketch, "E564", {"center": v(-25.4, -127) * mm, "radius": 8 * mm});
            skCircle(sketch, "E565", {"center": v(25.4, -127) * mm, "radius": 8 * mm});
            skCircle(sketch, "E566", {"center": v(76.2, -127) * mm, "radius": 8 * mm});
            skCircle(sketch, "E567", {"center": v(127, -127) * mm, "radius": 8 * mm});
            skCircle(sketch, "E568", {"center": v(177.8, -127) * mm, "radius": 8 * mm});
            skCircle(sketch, "E569", {"center": v(228.6, -127) * mm, "radius": 8 * mm});
            skCircle(sketch, "E570", {"center": v(279.4, -127) * mm, "radius": 8 * mm});
            skCircle(sketch, "E571", {"center": v(330.2, -127) * mm, "radius": 8 * mm});
            skCircle(sketch, "E572", {"center": v(381, -127) * mm, "radius": 8 * mm});
            skCircle(sketch, "E573", {"center": v(431.8, -127) * mm, "radius": 8 * mm});
            skCircle(sketch, "E574", {"center": v(431.8, -177.8) * mm, "radius": 8 * mm});
            skCircle(sketch, "E575", {"center": v(381, -177.8) * mm, "radius": 8 * mm});
            skCircle(sketch, "E576", {"center": v(330.2, -177.8) * mm, "radius": 8 * mm});
            skCircle(sketch, "E577", {"center": v(279.4, -177.8) * mm, "radius": 8 * mm});
            skCircle(sketch, "E578", {"center": v(228.6, -177.8) * mm, "radius": 8 * mm});
            skCircle(sketch, "E579", {"center": v(177.8, -177.8) * mm, "radius": 8 * mm});
            skCircle(sketch, "E580", {"center": v(127, -177.8) * mm, "radius": 8 * mm});
            skCircle(sketch, "E581", {"center": v(76.2, -177.8) * mm, "radius": 8 * mm});
            skCircle(sketch, "E582", {"center": v(25.4, -177.8) * mm, "radius": 8 * mm});
            skCircle(sketch, "E583", {"center": v(-25.4, -177.8) * mm, "radius": 8 * mm});
            skCircle(sketch, "E584", {"center": v(-76.2, -177.8) * mm, "radius": 8 * mm});
            skCircle(sketch, "E585", {"center": v(-127, -177.8) * mm, "radius": 8 * mm});
            skCircle(sketch, "E586", {"center": v(-177.8, -177.8) * mm, "radius": 8 * mm});
            skCircle(sketch, "E587", {"center": v(-228.6, -177.8) * mm, "radius": 8 * mm});
            skCircle(sketch, "E588", {"center": v(-279.4, -177.8) * mm, "radius": 8 * mm});
            skCircle(sketch, "E589", {"center": v(-330.2, -177.8) * mm, "radius": 8 * mm});
            skCircle(sketch, "E590", {"center": v(-381, -177.8) * mm, "radius": 8 * mm});
            skCircle(sketch, "E591", {"center": v(-431.8, -177.8) * mm, "radius": 8 * mm});
            skCircle(sketch, "E592", {"center": v(-431.8, -228.6) * mm, "radius": 8 * mm});
            skCircle(sketch, "E593", {"center": v(-381, -228.6) * mm, "radius": 8 * mm});
            skCircle(sketch, "E594", {"center": v(-330.2, -228.6) * mm, "radius": 8 * mm});
            skCircle(sketch, "E595", {"center": v(-279.4, -228.6) * mm, "radius": 8 * mm});
            skCircle(sketch, "E596", {"center": v(-228.6, -228.6) * mm, "radius": 8 * mm});
            skCircle(sketch, "E597", {"center": v(-177.8, -228.6) * mm, "radius": 8 * mm});
            skCircle(sketch, "E598", {"center": v(-127, -228.6) * mm, "radius": 8 * mm});
            skCircle(sketch, "E599", {"center": v(-76.2, -228.6) * mm, "radius": 8 * mm});
            skCircle(sketch, "E600", {"center": v(-25.4, -228.6) * mm, "radius": 8 * mm});
            skCircle(sketch, "E601", {"center": v(25.4, -228.6) * mm, "radius": 8 * mm});
            skCircle(sketch, "E602", {"center": v(76.2, -228.6) * mm, "radius": 8 * mm});
            skCircle(sketch, "E603", {"center": v(127, -228.6) * mm, "radius": 8 * mm});
            skCircle(sketch, "E604", {"center": v(177.8, -228.6) * mm, "radius": 8 * mm});
            skCircle(sketch, "E605", {"center": v(228.6, -228.6) * mm, "radius": 8 * mm});
            skCircle(sketch, "E606", {"center": v(279.4, -228.6) * mm, "radius": 8 * mm});
            skCircle(sketch, "E607", {"center": v(330.2, -228.6) * mm, "radius": 8 * mm});
            skCircle(sketch, "E608", {"center": v(381, -228.6) * mm, "radius": 8 * mm});
            skCircle(sketch, "E609", {"center": v(431.8, -228.6) * mm, "radius": 8 * mm});
            skCircle(sketch, "E610", {"center": v(-431.8, -279.4) * mm, "radius": 8 * mm});
            skCircle(sketch, "E611", {"center": v(-381, -279.4) * mm, "radius": 8 * mm});
            skCircle(sketch, "E612", {"center": v(-330.2, -279.4) * mm, "radius": 8 * mm});
            skCircle(sketch, "E613", {"center": v(-279.4, -279.4) * mm, "radius": 8 * mm});
            skCircle(sketch, "E614", {"center": v(-228.6, -279.4) * mm, "radius": 8 * mm});
            skCircle(sketch, "E615", {"center": v(-177.8, -279.4) * mm, "radius": 8 * mm});
            skCircle(sketch, "E616", {"center": v(-127, -279.4) * mm, "radius": 8 * mm});
            skCircle(sketch, "E617", {"center": v(-76.2, -279.4) * mm, "radius": 8 * mm});
            skCircle(sketch, "E618", {"center": v(-25.4, -279.4) * mm, "radius": 8 * mm});
            skCircle(sketch, "E619", {"center": v(25.4, -279.4) * mm, "radius": 8 * mm});
            skCircle(sketch, "E620", {"center": v(76.2, -279.4) * mm, "radius": 8 * mm});
            skCircle(sketch, "E621", {"center": v(127, -279.4) * mm, "radius": 8 * mm});
            skCircle(sketch, "E622", {"center": v(-431.8, -330.2) * mm, "radius": 8 * mm});
            skCircle(sketch, "E623", {"center": v(-381, -330.2) * mm, "radius": 8 * mm});
            skCircle(sketch, "E624", {"center": v(-330.2, -330.2) * mm, "radius": 8 * mm});
            skCircle(sketch, "E625", {"center": v(-279.4, -330.2) * mm, "radius": 8 * mm});
            skCircle(sketch, "E626", {"center": v(-228.6, -330.2) * mm, "radius": 8 * mm});
            skCircle(sketch, "E627", {"center": v(-177.8, -330.2) * mm, "radius": 8 * mm});
            skCircle(sketch, "E628", {"center": v(-127, -330.2) * mm, "radius": 8 * mm});
            skCircle(sketch, "E629", {"center": v(-76.2, -330.2) * mm, "radius": 8 * mm});
            skCircle(sketch, "E630", {"center": v(-25.4, -330.2) * mm, "radius": 8 * mm});
            skCircle(sketch, "E631", {"center": v(25.4, -330.2) * mm, "radius": 8 * mm});
            skCircle(sketch, "E632", {"center": v(76.2, -330.2) * mm, "radius": 8 * mm});
            skCircle(sketch, "E633", {"center": v(127, -330.2) * mm, "radius": 8 * mm});
            skCircle(sketch, "E634", {"center": v(177.8, -330.2) * mm, "radius": 8 * mm});
            skCircle(sketch, "E635", {"center": v(-431.8, -381) * mm, "radius": 8 * mm});
            skCircle(sketch, "E636", {"center": v(-381, -381) * mm, "radius": 8 * mm});
            skCircle(sketch, "E637", {"center": v(-330.2, -381) * mm, "radius": 8 * mm});
            skCircle(sketch, "E638", {"center": v(-279.4, -381) * mm, "radius": 8 * mm});
            skCircle(sketch, "E639", {"center": v(-228.6, -381) * mm, "radius": 8 * mm});
            skCircle(sketch, "E640", {"center": v(-177.8, -381) * mm, "radius": 8 * mm});
            skCircle(sketch, "E641", {"center": v(-127, -381) * mm, "radius": 8 * mm});
            skCircle(sketch, "E642", {"center": v(-76.2, -381) * mm, "radius": 8 * mm});
            skCircle(sketch, "E643", {"center": v(-25.4, -381) * mm, "radius": 8 * mm});
            skCircle(sketch, "E644", {"center": v(25.4, -381) * mm, "radius": 8 * mm});
            skCircle(sketch, "E645", {"center": v(76.2, -381) * mm, "radius": 8 * mm});
            skCircle(sketch, "E646", {"center": v(127, -381) * mm, "radius": 8 * mm});
            skCircle(sketch, "E647", {"center": v(177.8, -381) * mm, "radius": 8 * mm});
            skCircle(sketch, "E648", {"center": v(-431.8, -431.8) * mm, "radius": 8 * mm});
            skCircle(sketch, "E649", {"center": v(-381, -431.8) * mm, "radius": 8 * mm});
            skCircle(sketch, "E650", {"center": v(-330.2, -431.8) * mm, "radius": 8 * mm});
            skCircle(sketch, "E651", {"center": v(-279.4, -431.8) * mm, "radius": 8 * mm});
            skCircle(sketch, "E652", {"center": v(-228.6, -431.8) * mm, "radius": 8 * mm});
            skCircle(sketch, "E653", {"center": v(-177.8, -431.8) * mm, "radius": 8 * mm});
            skCircle(sketch, "E654", {"center": v(-127, -431.8) * mm, "radius": 8 * mm});
            skCircle(sketch, "E655", {"center": v(-76.2, -431.8) * mm, "radius": 8 * mm});
            skCircle(sketch, "E656", {"center": v(-25.4, -431.8) * mm, "radius": 8 * mm});
            skCircle(sketch, "E657", {"center": v(25.4, -431.8) * mm, "radius": 8 * mm});
            skCircle(sketch, "E658", {"center": v(76.2, -431.8) * mm, "radius": 8 * mm});
            skCircle(sketch, "E659", {"center": v(127, -431.8) * mm, "radius": 8 * mm});
            skCircle(sketch, "E660", {"center": v(177.8, -431.8) * mm, "radius": 8 * mm});
            skCircle(sketch, "E661", {"center": v(330.2, -381) * mm, "radius": 8 * mm});
            skCircle(sketch, "E662", {"center": v(228.6, -279.4) * mm, "radius": 8 * mm});
            skCircle(sketch, "E663", {"center": v(279.4, -279.4) * mm, "radius": 8 * mm});
            skCircle(sketch, "E664", {"center": v(330.2, -279.4) * mm, "radius": 8 * mm});
            skCircle(sketch, "E665", {"center": v(381, -279.4) * mm, "radius": 8 * mm});
            skCircle(sketch, "E666", {"center": v(431.8, -279.4) * mm, "radius": 8 * mm});
            skCircle(sketch, "E667", {"center": v(228.6, -330.2) * mm, "radius": 8 * mm});
            skCircle(sketch, "E668", {"center": v(279.4, -330.2) * mm, "radius": 8 * mm});
            skCircle(sketch, "E669", {"center": v(330.2, -330.2) * mm, "radius": 8 * mm});
            skCircle(sketch, "E670", {"center": v(381, -330.2) * mm, "radius": 8 * mm});
            skCircle(sketch, "E671", {"center": v(431.8, -330.2) * mm, "radius": 8 * mm});
            skCircle(sketch, "E672", {"center": v(228.6, -381) * mm, "radius": 8 * mm});
            skCircle(sketch, "E673", {"center": v(279.4, -381) * mm, "radius": 8 * mm});
            skCircle(sketch, "E674", {"center": v(381, -381) * mm, "radius": 8 * mm});
            skCircle(sketch, "E675", {"center": v(431.8, -381) * mm, "radius": 8 * mm});
            skCircle(sketch, "E676", {"center": v(228.6, -431.8) * mm, "radius": 8 * mm});
            skCircle(sketch, "E677", {"center": v(279.4, -431.8) * mm, "radius": 8 * mm});
            skCircle(sketch, "E678", {"center": v(330.2, -431.8) * mm, "radius": 8 * mm});
            skCircle(sketch, "E679", {"center": v(381, -431.8) * mm, "radius": 8 * mm});
            skCircle(sketch, "E680", {"center": v(431.8, -431.8) * mm, "radius": 8 * mm});
            skCircle(sketch, "E681", {"center": v(177.8, -279.4) * mm, "radius": 8 * mm});
            skSolve(sketch);
        }
        {
            var Q0;
            Q0=sQuery(id+"F2.wireOp",VERTEX,"E37.center");
            var Q1;
            Q1=sQuery(id+"F2.wireOp",VERTEX,"E38");
            var Q2;
            Q2=sQuery(id+"F2.wireOp",VERTEX,"E39");
            var Q3;
            Q3=sQuery(id+"F2.wireOp",VERTEX,"E49.center");
            var Q4;
            Q4=sQuery(id+"F2.wireOp",VERTEX,"E41");
            var Q5;
            Q5=sQuery(id+"F2.wireOp",VERTEX,"E369.center");
            var Q6;
            Q6=sQuery(id+"F2.wireOp",VERTEX,"E75");
            var Q7;
            Q7=sQuery(id+"F2.wireOp",VERTEX,"E371.center");
            var Q8;
            Q8=sQuery(id+"F2.wireOp",VERTEX,"E85");
            var Q9;
            Q9=sQuery(id+"F2.wireOp",VERTEX,"E90");
            var Q10;
            Q10=sQuery(id+"F2.wireOp",VERTEX,"E95");
            var Q11;
            Q11=sQuery(id+"F2.wireOp",VERTEX,"E100");
            var Q12;
            Q12=sQuery(id+"F2.wireOp",VERTEX,"E101");
            var Q13;
            Q13=sQuery(id+"F2.wireOp",VERTEX,"E102");
            var Q14;
            Q14=sQuery(id+"F2.wireOp",VERTEX,"E103");
            var Q15;
            Q15=sQuery(id+"F2.wireOp",VERTEX,"E104");
            var Q16;
            Q16=sQuery(id+"F2.wireOp",VERTEX,"E422.center");
            var Q17;
            Q17=sQuery(id+"F2.wireOp",VERTEX,"E429.center");
            var Q18;
            Q18=sQuery(id+"F2.wireOp",VERTEX,"E428.center");
            var Q19;
            Q19=sQuery(id+"F2.wireOp",VERTEX,"E112");
            var Q20;
            Q20=sQuery(id+"F2.wireOp",VERTEX,"E111");
            var Q21;
            Q21=sQuery(id+"F2.wireOp",VERTEX,"E110");
            var Q22;
            Q22=sQuery(id+"F2.wireOp",VERTEX,"E411.center");
            var Q23;
            Q23=sQuery(id+"F2.wireOp",VERTEX,"E108");
            var Q24;
            Q24=sQuery(id+"F2.wireOp",VERTEX,"E399.center");
            var Q25;
            Q25=sQuery(id+"F2.wireOp",VERTEX,"E96");
            var Q26;
            Q26=sQuery(id+"F2.wireOp",VERTEX,"E397.center");
            var Q27;
            Q27=sQuery(id+"F2.wireOp",VERTEX,"E373.center");
            var Q28;
            Q28=sQuery(id+"F2.wireOp",VERTEX,"E374.center");
            var Q29;
            Q29=sQuery(id+"F2.wireOp",VERTEX,"E76");
            var Q30;
            Q30=sQuery(id+"F2.wireOp",VERTEX,"E395.center");
            var Q31;
            Q31=sQuery(id+"F2.wireOp",VERTEX,"E42");
            var Q32;
            Q32=sQuery(id+"F2.wireOp",VERTEX,"E43");
            var Q33;
            Q33=sQuery(id+"F2.wireOp",VERTEX,"E44");
            var Q34;
            Q34=sQuery(id+"F2.wireOp",VERTEX,"E45");
            var Q35;
            Q35=sQuery(id+"F2.wireOp",VERTEX,"E46");
            var Q36;
            Q36=sQuery(id+"F2.wireOp",VERTEX,"E55.center");
            var Q37;
            Q37=sQuery(id+"F2.wireOp",VERTEX,"E56.center");
            var Q38;
            Q38=sQuery(id+"F2.wireOp",VERTEX,"E57");
            var Q39;
            Q39=sQuery(id+"F2.wireOp",VERTEX,"E58");
            var Q40;
            Q40=sQuery(id+"F2.wireOp",VERTEX,"E59");
            var Q41;
            Q41=sQuery(id+"F2.wireOp",VERTEX,"E379.center");
            var Q42;
            Q42=sQuery(id+"F2.wireOp",VERTEX,"E77");
            var Q43;
            Q43=sQuery(id+"F2.wireOp",VERTEX,"E381.center");
            var Q44;
            Q44=sQuery(id+"F2.wireOp",VERTEX,"E87");
            var Q45;
            Q45=sQuery(id+"F2.wireOp",VERTEX,"E400.center");
            var Q46;
            Q46=sQuery(id+"F2.wireOp",VERTEX,"E97");
            var Q47;
            Q47=sQuery(id+"F2.wireOp",VERTEX,"E114");
            var Q48;
            Q48=sQuery(id+"F2.wireOp",VERTEX,"E115");
            var Q49;
            Q49=sQuery(id+"F2.wireOp",VERTEX,"E116");
            var Q50;
            Q50=sQuery(id+"F2.wireOp",VERTEX,"E117");
            var Q51;
            Q51=sQuery(id+"F2.wireOp",VERTEX,"E118");
            var Q52;
            Q52=sQuery(id+"F2.wireOp",VERTEX,"E119");
            var Q53;
            Q53=sQuery(id+"F2.wireOp",VERTEX,"E120");
            var Q54;
            Q54=sQuery(id+"F2.wireOp",VERTEX,"E426.center");
            var Q55;
            Q55=sQuery(id+"F2.wireOp",VERTEX,"E425.center");
            var Q56;
            Q56=sQuery(id+"F2.wireOp",VERTEX,"E421.center");
            var Q57;
            Q57=sQuery(id+"F2.wireOp",VERTEX,"E417.center");
            var Q58;
            Q58=sQuery(id+"F2.wireOp",VERTEX,"E123");
            var Q59;
            Q59=sQuery(id+"F2.wireOp",VERTEX,"E122");
            var Q60;
            Q60=sQuery(id+"F2.wireOp",VERTEX,"E121");
            var Q61;
            Q61=sQuery(id+"F2.wireOp",VERTEX,"E98");
            var Q62;
            Q62=sQuery(id+"F2.wireOp",VERTEX,"E93");
            var Q63;
            Q63=sQuery(id+"F2.wireOp",VERTEX,"E88");
            var Q64;
            Q64=sQuery(id+"F2.wireOp",VERTEX,"E83");
            var Q65;
            Q65=sQuery(id+"F2.wireOp",VERTEX,"E78");
            var Q66;
            Q66=sQuery(id+"F2.wireOp",VERTEX,"E386.center");
            var Q67;
            Q67=sQuery(id+"F2.wireOp",VERTEX,"E60");
            var Q68;
            Q68=sQuery(id+"F2.wireOp",VERTEX,"E61");
            var Q69;
            Q69=sQuery(id+"F2.wireOp",VERTEX,"E62");
            var Q70;
            Q70=sQuery(id+"F2.wireOp",VERTEX,"E63");
            var Q71;
            Q71=sQuery(id+"F2.wireOp",VERTEX,"E64");
            var Q72;
            Q72=makeQuery(id+"F1.opExtrude","SWEPT_BODY",BODY,{"disambiguationData":[OSD([sQuery(id+"F0.wireOp",EDGE,"E0.bottom"),sQuery(id+"F0.wireOp",EDGE,"E0.top"),sQuery(id+"F0.wireOp",EDGE,"E0.left"),sQuery(id+"F0.wireOp",EDGE,"E0.right")])]});
            hole(context, id + "F3", {"style" : HoleStyle.SIMPLE, "endStyle" : HoleEndStyle.THROUGH, "holeDiameter" : 16 * mm, "majorDiameter" : 6.35 * mm, "isTappedThrough" : true, "tappedDepth" : 12.7 * mm, "tapClearance" : 3, "locations" : qUnion([Q0, Q1, Q2, Q3, Q4, Q5, Q6, Q7, Q8, Q9, Q10, Q11, Q12, Q13, Q14, Q15, Q16, Q17, Q18, Q19, Q20, Q21, Q22, Q23, Q24, Q25, Q26, Q27, Q28, Q29, Q30, Q31, Q32, Q33, Q34, Q35, Q36, Q37, Q38, Q39, Q40, Q41, Q42, Q43, Q44, Q45, Q46, Q47, Q48, Q49, Q50, Q51, Q52, Q53, Q54, Q55, Q56, Q57, Q58, Q59, Q60, Q61, Q62, Q63, Q64, Q65, Q66, Q67, Q68, Q69, Q70, Q71]), "scope" : qUnion([Q72])});
        }
        {
            var Q0;
            Q0=sQuery(id+"F2.wireOp",VERTEX,"E65");
            var Q1;
            Q1=sQuery(id+"F2.wireOp",VERTEX,"E135");
            var Q2;
            Q2=sQuery(id+"F2.wireOp",VERTEX,"E466.center");
            var Q3;
            Q3=sQuery(id+"F2.wireOp",VERTEX,"E188");
            var Q4;
            Q4=sQuery(id+"F2.wireOp",VERTEX,"E187");
            var Q5;
            Q5=sQuery(id+"F2.wireOp",VERTEX,"E154");
            var Q6;
            Q6=sQuery(id+"F2.wireOp",VERTEX,"E136");
            var Q7;
            Q7=sQuery(id+"F2.wireOp",VERTEX,"E66");
            var Q8;
            Q8=sQuery(id+"F2.wireOp",VERTEX,"E67");
            var Q9;
            Q9=sQuery(id+"F2.wireOp",VERTEX,"E137");
            var Q10;
            Q10=sQuery(id+"F2.wireOp",VERTEX,"E155");
            var Q11;
            Q11=sQuery(id+"F2.wireOp",VERTEX,"E186");
            var Q12;
            Q12=sQuery(id+"F2.wireOp",VERTEX,"E185");
            var Q13;
            Q13=sQuery(id+"F2.wireOp",VERTEX,"E156");
            var Q14;
            Q14=sQuery(id+"F2.wireOp",VERTEX,"E462.center");
            var Q15;
            Q15=sQuery(id+"F2.wireOp",VERTEX,"E68");
            var Q16;
            Q16=sQuery(id+"F2.wireOp",VERTEX,"E69");
            var Q17;
            Q17=sQuery(id+"F2.wireOp",VERTEX,"E139");
            var Q18;
            Q18=sQuery(id+"F2.wireOp",VERTEX,"E157");
            var Q19;
            Q19=sQuery(id+"F2.wireOp",VERTEX,"E184");
            var Q20;
            Q20=sQuery(id+"F2.wireOp",VERTEX,"E183");
            var Q21;
            Q21=sQuery(id+"F2.wireOp",VERTEX,"E471.center");
            var Q22;
            Q22=sQuery(id+"F2.wireOp",VERTEX,"E140");
            var Q23;
            Q23=sQuery(id+"F2.wireOp",VERTEX,"E435.center");
            var Q24;
            Q24=sQuery(id+"F2.wireOp",VERTEX,"E79");
            var Q25;
            Q25=sQuery(id+"F2.wireOp",VERTEX,"E141");
            var Q26;
            Q26=sQuery(id+"F2.wireOp",VERTEX,"E159");
            var Q27;
            Q27=sQuery(id+"F2.wireOp",VERTEX,"E182");
            var Q28;
            Q28=sQuery(id+"F2.wireOp",VERTEX,"E181");
            var Q29;
            Q29=sQuery(id+"F2.wireOp",VERTEX,"E160");
            var Q30;
            Q30=sQuery(id+"F2.wireOp",VERTEX,"E458.center");
            var Q31;
            Q31=sQuery(id+"F2.wireOp",VERTEX,"E437.center");
            var Q32;
            Q32=sQuery(id+"F2.wireOp",VERTEX,"E438.center");
            var Q33;
            Q33=sQuery(id+"F2.wireOp",VERTEX,"E143");
            var Q34;
            Q34=sQuery(id+"F2.wireOp",VERTEX,"E161");
            var Q35;
            Q35=sQuery(id+"F2.wireOp",VERTEX,"E180");
            var Q36;
            Q36=sQuery(id+"F2.wireOp",VERTEX,"E492.center");
            var Q37;
            Q37=sQuery(id+"F2.wireOp",VERTEX,"E475.center");
            var Q38;
            Q38=sQuery(id+"F2.wireOp",VERTEX,"E145");
            var Q39;
            Q39=sQuery(id+"F2.wireOp",VERTEX,"E94");
            var Q40;
            Q40=sQuery(id+"F2.wireOp",VERTEX,"E99");
            var Q41;
            Q41=sQuery(id+"F2.wireOp",VERTEX,"E144");
            var Q42;
            Q42=sQuery(id+"F2.wireOp",VERTEX,"E163");
            var Q43;
            Q43=sQuery(id+"F2.wireOp",VERTEX,"E178");
            var Q44;
            Q44=sQuery(id+"F2.wireOp",VERTEX,"E177");
            var Q45;
            Q45=sQuery(id+"F2.wireOp",VERTEX,"E477.center");
            var Q46;
            Q46=sQuery(id+"F2.wireOp",VERTEX,"E146");
            var Q47;
            Q47=sQuery(id+"F2.wireOp",VERTEX,"E128");
            var Q48;
            Q48=sQuery(id+"F2.wireOp",VERTEX,"E129");
            var Q49;
            Q49=sQuery(id+"F2.wireOp",VERTEX,"E147");
            var Q50;
            Q50=sQuery(id+"F2.wireOp",VERTEX,"E478.center");
            var Q51;
            Q51=sQuery(id+"F2.wireOp",VERTEX,"E176");
            var Q52;
            Q52=sQuery(id+"F2.wireOp",VERTEX,"E175");
            var Q53;
            Q53=sQuery(id+"F2.wireOp",VERTEX,"E166");
            var Q54;
            Q54=sQuery(id+"F2.wireOp",VERTEX,"E148");
            var Q55;
            Q55=sQuery(id+"F2.wireOp",VERTEX,"E130");
            var Q56;
            Q56=sQuery(id+"F2.wireOp",VERTEX,"E131");
            var Q57;
            Q57=sQuery(id+"F2.wireOp",VERTEX,"E149");
            var Q58;
            Q58=sQuery(id+"F2.wireOp",VERTEX,"E480.center");
            var Q59;
            Q59=sQuery(id+"F2.wireOp",VERTEX,"E174");
            var Q60;
            Q60=sQuery(id+"F2.wireOp",VERTEX,"E173");
            var Q61;
            Q61=sQuery(id+"F2.wireOp",VERTEX,"E168");
            var Q62;
            Q62=sQuery(id+"F2.wireOp",VERTEX,"E450.center");
            var Q63;
            Q63=sQuery(id+"F2.wireOp",VERTEX,"E132");
            var Q64;
            Q64=sQuery(id+"F2.wireOp",VERTEX,"E133");
            var Q65;
            Q65=sQuery(id+"F2.wireOp",VERTEX,"E449.center");
            var Q66;
            Q66=sQuery(id+"F2.wireOp",VERTEX,"E482.center");
            var Q67;
            Q67=sQuery(id+"F2.wireOp",VERTEX,"E172");
            var Q68;
            Q68=sQuery(id+"F2.wireOp",VERTEX,"E171");
            var Q69;
            Q69=sQuery(id+"F2.wireOp",VERTEX,"E170");
            var Q70;
            Q70=sQuery(id+"F2.wireOp",VERTEX,"E152");
            var Q71;
            Q71=sQuery(id+"F2.wireOp",VERTEX,"E134");
            var Q72;
            Q72=makeQuery(id+"F1.opExtrude","SWEPT_BODY",BODY,{"disambiguationData":[OSD([sQuery(id+"F0.wireOp",EDGE,"E0.bottom"),sQuery(id+"F0.wireOp",EDGE,"E0.top"),sQuery(id+"F0.wireOp",EDGE,"E0.left"),sQuery(id+"F0.wireOp",EDGE,"E0.right")])]});
            hole(context, id + "F4", {"style" : HoleStyle.SIMPLE, "endStyle" : HoleEndStyle.THROUGH, "holeDiameter" : 16 * mm, "majorDiameter" : 6.35 * mm, "isTappedThrough" : true, "tappedDepth" : 12.7 * mm, "tapClearance" : 3, "locations" : qUnion([Q0, Q1, Q2, Q3, Q4, Q5, Q6, Q7, Q8, Q9, Q10, Q11, Q12, Q13, Q14, Q15, Q16, Q17, Q18, Q19, Q20, Q21, Q22, Q23, Q24, Q25, Q26, Q27, Q28, Q29, Q30, Q31, Q32, Q33, Q34, Q35, Q36, Q37, Q38, Q39, Q40, Q41, Q42, Q43, Q44, Q45, Q46, Q47, Q48, Q49, Q50, Q51, Q52, Q53, Q54, Q55, Q56, Q57, Q58, Q59, Q60, Q61, Q62, Q63, Q64, Q65, Q66, Q67, Q68, Q69, Q70, Q71]), "scope" : qUnion([Q72])});
        }
        {
            var Q0;
            Q0=sQuery(id+"F2.wireOp",VERTEX,"E189");
            var Q1;
            Q1=sQuery(id+"F2.wireOp",VERTEX,"E224");
            var Q2;
            Q2=sQuery(id+"F2.wireOp",VERTEX,"E225");
            var Q3;
            Q3=sQuery(id+"F2.wireOp",VERTEX,"E260");
            var Q4;
            Q4=sQuery(id+"F2.wireOp",VERTEX,"E259");
            var Q5;
            Q5=sQuery(id+"F2.wireOp",VERTEX,"E554.center");
            var Q6;
            Q6=sQuery(id+"F2.wireOp",VERTEX,"E549.center");
            var Q7;
            Q7=sQuery(id+"F2.wireOp",VERTEX,"E190");
            var Q8;
            Q8=sQuery(id+"F2.wireOp",VERTEX,"E191");
            var Q9;
            Q9=sQuery(id+"F2.wireOp",VERTEX,"E222");
            var Q10;
            Q10=sQuery(id+"F2.wireOp",VERTEX,"E227");
            var Q11;
            Q11=sQuery(id+"F2.wireOp",VERTEX,"E258");
            var Q12;
            Q12=sQuery(id+"F2.wireOp",VERTEX,"E559.center");
            var Q13;
            Q13=sQuery(id+"F2.wireOp",VERTEX,"E228");
            var Q14;
            Q14=sQuery(id+"F2.wireOp",VERTEX,"E551.center");
            var Q15;
            Q15=sQuery(id+"F2.wireOp",VERTEX,"E192");
            var Q16;
            Q16=sQuery(id+"F2.wireOp",VERTEX,"E506.center");
            var Q17;
            Q17=sQuery(id+"F2.wireOp",VERTEX,"E220");
            var Q18;
            Q18=sQuery(id+"F2.wireOp",VERTEX,"E229");
            var Q19;
            Q19=sQuery(id+"F2.wireOp",VERTEX,"E256");
            var Q20;
            Q20=sQuery(id+"F2.wireOp",VERTEX,"E561.center");
            var Q21;
            Q21=sQuery(id+"F2.wireOp",VERTEX,"E230");
            var Q22;
            Q22=sQuery(id+"F2.wireOp",VERTEX,"E219");
            var Q23;
            Q23=sQuery(id+"F2.wireOp",VERTEX,"E194");
            var Q24;
            Q24=sQuery(id+"F2.wireOp",VERTEX,"E195");
            var Q25;
            Q25=sQuery(id+"F2.wireOp",VERTEX,"E218");
            var Q26;
            Q26=sQuery(id+"F2.wireOp",VERTEX,"E231");
            var Q27;
            Q27=sQuery(id+"F2.wireOp",VERTEX,"E254");
            var Q28;
            Q28=sQuery(id+"F2.wireOp",VERTEX,"E563.center");
            var Q29;
            Q29=sQuery(id+"F2.wireOp",VERTEX,"E232");
            var Q30;
            Q30=sQuery(id+"F2.wireOp",VERTEX,"E523.center");
            var Q31;
            Q31=sQuery(id+"F2.wireOp",VERTEX,"E196");
            var Q32;
            Q32=sQuery(id+"F2.wireOp",VERTEX,"E197");
            var Q33;
            Q33=sQuery(id+"F2.wireOp",VERTEX,"E216");
            var Q34;
            Q34=sQuery(id+"F2.wireOp",VERTEX,"E233");
            var Q35;
            Q35=sQuery(id+"F2.wireOp",VERTEX,"E252");
            var Q36;
            Q36=sQuery(id+"F2.wireOp",VERTEX,"E565.center");
            var Q37;
            Q37=sQuery(id+"F2.wireOp",VERTEX,"E234");
            var Q38;
            Q38=sQuery(id+"F2.wireOp",VERTEX,"E215");
            var Q39;
            Q39=sQuery(id+"F2.wireOp",VERTEX,"E198");
            var Q40;
            Q40=sQuery(id+"F2.wireOp",VERTEX,"E512.center");
            var Q41;
            Q41=sQuery(id+"F2.wireOp",VERTEX,"E526.center");
            var Q42;
            Q42=sQuery(id+"F2.wireOp",VERTEX,"E235");
            var Q43;
            Q43=sQuery(id+"F2.wireOp",VERTEX,"E250");
            var Q44;
            Q44=sQuery(id+"F2.wireOp",VERTEX,"E249");
            var Q45;
            Q45=sQuery(id+"F2.wireOp",VERTEX,"E236");
            var Q46;
            Q46=sQuery(id+"F2.wireOp",VERTEX,"E213");
            var Q47;
            Q47=sQuery(id+"F2.wireOp",VERTEX,"E513.center");
            var Q48;
            Q48=sQuery(id+"F2.wireOp",VERTEX,"E201");
            var Q49;
            Q49=sQuery(id+"F2.wireOp",VERTEX,"E212");
            var Q50;
            Q50=sQuery(id+"F2.wireOp",VERTEX,"E237");
            var Q51;
            Q51=sQuery(id+"F2.wireOp",VERTEX,"E248");
            var Q52;
            Q52=sQuery(id+"F2.wireOp",VERTEX,"E247");
            var Q53;
            Q53=sQuery(id+"F2.wireOp",VERTEX,"E238");
            var Q54;
            Q54=sQuery(id+"F2.wireOp",VERTEX,"E211");
            var Q55;
            Q55=sQuery(id+"F2.wireOp",VERTEX,"E202");
            var Q56;
            Q56=sQuery(id+"F2.wireOp",VERTEX,"E203");
            var Q57;
            Q57=sQuery(id+"F2.wireOp",VERTEX,"E210");
            var Q58;
            Q58=sQuery(id+"F2.wireOp",VERTEX,"E239");
            var Q59;
            Q59=sQuery(id+"F2.wireOp",VERTEX,"E570.center");
            var Q60;
            Q60=sQuery(id+"F2.wireOp",VERTEX,"E245");
            var Q61;
            Q61=sQuery(id+"F2.wireOp",VERTEX,"E240");
            var Q62;
            Q62=sQuery(id+"F2.wireOp",VERTEX,"E209");
            var Q63;
            Q63=sQuery(id+"F2.wireOp",VERTEX,"E204");
            var Q64;
            Q64=sQuery(id+"F2.wireOp",VERTEX,"E518.center");
            var Q65;
            Q65=sQuery(id+"F2.wireOp",VERTEX,"E208");
            var Q66;
            Q66=sQuery(id+"F2.wireOp",VERTEX,"E241");
            var Q67;
            Q67=sQuery(id+"F2.wireOp",VERTEX,"E244");
            var Q68;
            Q68=sQuery(id+"F2.wireOp",VERTEX,"E573.center");
            var Q69;
            Q69=sQuery(id+"F2.wireOp",VERTEX,"E242");
            var Q70;
            Q70=sQuery(id+"F2.wireOp",VERTEX,"E533.center");
            var Q71;
            Q71=sQuery(id+"F2.wireOp",VERTEX,"E206");
            var Q72;
            Q72=makeQuery(id+"F1.opExtrude","SWEPT_BODY",BODY,{"disambiguationData":[OSD([sQuery(id+"F0.wireOp",EDGE,"E0.bottom"),sQuery(id+"F0.wireOp",EDGE,"E0.top"),sQuery(id+"F0.wireOp",EDGE,"E0.left"),sQuery(id+"F0.wireOp",EDGE,"E0.right")])]});
            hole(context, id + "F5", {"style" : HoleStyle.SIMPLE, "endStyle" : HoleEndStyle.THROUGH, "holeDiameter" : 16 * mm, "majorDiameter" : 6.35 * mm, "isTappedThrough" : true, "tappedDepth" : 12.7 * mm, "tapClearance" : 3, "locations" : qUnion([Q0, Q1, Q2, Q3, Q4, Q5, Q6, Q7, Q8, Q9, Q10, Q11, Q12, Q13, Q14, Q15, Q16, Q17, Q18, Q19, Q20, Q21, Q22, Q23, Q24, Q25, Q26, Q27, Q28, Q29, Q30, Q31, Q32, Q33, Q34, Q35, Q36, Q37, Q38, Q39, Q40, Q41, Q42, Q43, Q44, Q45, Q46, Q47, Q48, Q49, Q50, Q51, Q52, Q53, Q54, Q55, Q56, Q57, Q58, Q59, Q60, Q61, Q62, Q63, Q64, Q65, Q66, Q67, Q68, Q69, Q70, Q71]), "scope" : qUnion([Q72])});
        }
        {
            var Q0;
            Q0=sQuery(id+"F2.wireOp",VERTEX,"E591.center");
            var Q1;
            Q1=sQuery(id+"F2.wireOp",VERTEX,"E296");
            var Q2;
            Q2=sQuery(id+"F2.wireOp",VERTEX,"E297");
            var Q3;
            Q3=sQuery(id+"F2.wireOp",VERTEX,"E332");
            var Q4;
            Q4=sQuery(id+"F2.wireOp",VERTEX,"E590.center");
            var Q5;
            Q5=sQuery(id+"F2.wireOp",VERTEX,"E295");
            var Q6;
            Q6=sQuery(id+"F2.wireOp",VERTEX,"E298");
            var Q7;
            Q7=sQuery(id+"F2.wireOp",VERTEX,"E331");
            var Q8;
            Q8=sQuery(id+"F2.wireOp",VERTEX,"E263");
            var Q9;
            Q9=sQuery(id+"F2.wireOp",VERTEX,"E294");
            var Q10;
            Q10=sQuery(id+"F2.wireOp",VERTEX,"E299");
            var Q11;
            Q11=sQuery(id+"F2.wireOp",VERTEX,"E330");
            var Q12;
            Q12=sQuery(id+"F2.wireOp",VERTEX,"E625.center");
            var Q13;
            Q13=sQuery(id+"F2.wireOp",VERTEX,"E613.center");
            var Q14;
            Q14=sQuery(id+"F2.wireOp",VERTEX,"E293");
            var Q15;
            Q15=sQuery(id+"F2.wireOp",VERTEX,"E264");
            var Q16;
            Q16=sQuery(id+"F2.wireOp",VERTEX,"E265");
            var Q17;
            Q17=sQuery(id+"F2.wireOp",VERTEX,"E596.center");
            var Q18;
            Q18=sQuery(id+"F2.wireOp",VERTEX,"E614.center");
            var Q19;
            Q19=sQuery(id+"F2.wireOp",VERTEX,"E328");
            var Q20;
            Q20=sQuery(id+"F2.wireOp",VERTEX,"E327");
            var Q21;
            Q21=sQuery(id+"F2.wireOp",VERTEX,"E615.center");
            var Q22;
            Q22=sQuery(id+"F2.wireOp",VERTEX,"E291");
            var Q23;
            Q23=sQuery(id+"F2.wireOp",VERTEX,"E266");
            var Q24;
            Q24=sQuery(id+"F2.wireOp",VERTEX,"E267");
            var Q25;
            Q25=sQuery(id+"F2.wireOp",VERTEX,"E290");
            var Q26;
            Q26=sQuery(id+"F2.wireOp",VERTEX,"E303");
            var Q27;
            Q27=sQuery(id+"F2.wireOp",VERTEX,"E326");
            var Q28;
            Q28=sQuery(id+"F2.wireOp",VERTEX,"E629.center");
            var Q29;
            Q29=sQuery(id+"F2.wireOp",VERTEX,"E304");
            var Q30;
            Q30=sQuery(id+"F2.wireOp",VERTEX,"E289");
            var Q31;
            Q31=sQuery(id+"F2.wireOp",VERTEX,"E268");
            var Q32;
            Q32=sQuery(id+"F2.wireOp",VERTEX,"E269");
            var Q33;
            Q33=sQuery(id+"F2.wireOp",VERTEX,"E288");
            var Q34;
            Q34=sQuery(id+"F2.wireOp",VERTEX,"E305");
            var Q35;
            Q35=sQuery(id+"F2.wireOp",VERTEX,"E324");
            var Q36;
            Q36=sQuery(id+"F2.wireOp",VERTEX,"E323");
            var Q37;
            Q37=sQuery(id+"F2.wireOp",VERTEX,"E306");
            var Q38;
            Q38=sQuery(id+"F2.wireOp",VERTEX,"E287");
            var Q39;
            Q39=sQuery(id+"F2.wireOp",VERTEX,"E270");
            var Q40;
            Q40=sQuery(id+"F2.wireOp",VERTEX,"E271");
            var Q41;
            Q41=sQuery(id+"F2.wireOp",VERTEX,"E286");
            var Q42;
            Q42=sQuery(id+"F2.wireOp",VERTEX,"E307");
            var Q43;
            Q43=sQuery(id+"F2.wireOp",VERTEX,"E322");
            var Q44;
            Q44=sQuery(id+"F2.wireOp",VERTEX,"E633.center");
            var Q45;
            Q45=sQuery(id+"F2.wireOp",VERTEX,"E308");
            var Q46;
            Q46=sQuery(id+"F2.wireOp",VERTEX,"E285");
            var Q47;
            Q47=sQuery(id+"F2.wireOp",VERTEX,"E272");
            var Q48;
            Q48=sQuery(id+"F2.wireOp",VERTEX,"E273");
            var Q49;
            Q49=sQuery(id+"F2.wireOp",VERTEX,"E284");
            var Q50;
            Q50=sQuery(id+"F2.wireOp",VERTEX,"E320");
            var Q51;
            Q51=sQuery(id+"F2.wireOp",VERTEX,"E681.center");
            var Q52;
            Q52=sQuery(id+"F2.wireOp",VERTEX,"E667.center");
            var Q53;
            Q53=sQuery(id+"F2.wireOp",VERTEX,"E310");
            var Q54;
            Q54=sQuery(id+"F2.wireOp",VERTEX,"E283");
            var Q55;
            Q55=sQuery(id+"F2.wireOp",VERTEX,"E274");
            var Q56;
            Q56=sQuery(id+"F2.wireOp",VERTEX,"E275");
            var Q57;
            Q57=sQuery(id+"F2.wireOp",VERTEX,"E282");
            var Q58;
            Q58=sQuery(id+"F2.wireOp",VERTEX,"E311");
            var Q59;
            Q59=sQuery(id+"F2.wireOp",VERTEX,"E318");
            var Q60;
            Q60=sQuery(id+"F2.wireOp",VERTEX,"E317");
            var Q61;
            Q61=sQuery(id+"F2.wireOp",VERTEX,"E313");
            var Q62;
            Q62=sQuery(id+"F2.wireOp",VERTEX,"E279");
            var Q63;
            Q63=sQuery(id+"F2.wireOp",VERTEX,"E277");
            var Q64;
            Q64=sQuery(id+"F2.wireOp",VERTEX,"E281");
            var Q65;
            Q65=sQuery(id+"F2.wireOp",VERTEX,"E315");
            var Q66;
            Q66=sQuery(id+"F2.wireOp",VERTEX,"E316");
            var Q67;
            Q67=sQuery(id+"F2.wireOp",VERTEX,"E314");
            var Q68;
            Q68=sQuery(id+"F2.wireOp",VERTEX,"E280");
            var Q69;
            Q69=sQuery(id+"F2.wireOp",VERTEX,"E276");
            var Q70;
            Q70=sQuery(id+"F2.wireOp",VERTEX,"E278");
            var Q71;
            Q71=sQuery(id+"F2.wireOp",VERTEX,"E664.center");
            var Q72;
            Q72=makeQuery(id+"F1.opExtrude","SWEPT_BODY",BODY,{"disambiguationData":[OSD([sQuery(id+"F0.wireOp",EDGE,"E0.bottom"),sQuery(id+"F0.wireOp",EDGE,"E0.top"),sQuery(id+"F0.wireOp",EDGE,"E0.left"),sQuery(id+"F0.wireOp",EDGE,"E0.right")])]});
            hole(context, id + "F6", {"style" : HoleStyle.SIMPLE, "endStyle" : HoleEndStyle.THROUGH, "holeDiameter" : 16 * mm, "majorDiameter" : 6.35 * mm, "isTappedThrough" : true, "tappedDepth" : 12.7 * mm, "tapClearance" : 3, "locations" : qUnion([Q0, Q1, Q2, Q3, Q4, Q5, Q6, Q7, Q8, Q9, Q10, Q11, Q12, Q13, Q14, Q15, Q16, Q17, Q18, Q19, Q20, Q21, Q22, Q23, Q24, Q25, Q26, Q27, Q28, Q29, Q30, Q31, Q32, Q33, Q34, Q35, Q36, Q37, Q38, Q39, Q40, Q41, Q42, Q43, Q44, Q45, Q46, Q47, Q48, Q49, Q50, Q51, Q52, Q53, Q54, Q55, Q56, Q57, Q58, Q59, Q60, Q61, Q62, Q63, Q64, Q65, Q66, Q67, Q68, Q69, Q70, Q71]), "scope" : qUnion([Q72])});
        }
        {
            var Q0;
            Q0=sQuery(id+"F2.wireOp",VERTEX,"E635.center");
            var Q1;
            Q1=sQuery(id+"F2.wireOp",VERTEX,"E334");
            var Q2;
            Q2=sQuery(id+"F2.wireOp",VERTEX,"E335");
            var Q3;
            Q3=sQuery(id+"F2.wireOp",VERTEX,"E336");
            var Q4;
            Q4=sQuery(id+"F2.wireOp",VERTEX,"E337");
            var Q5;
            Q5=sQuery(id+"F2.wireOp",VERTEX,"E338");
            var Q6;
            Q6=sQuery(id+"F2.wireOp",VERTEX,"E641.center");
            var Q7;
            Q7=sQuery(id+"F2.wireOp",VERTEX,"E340");
            var Q8;
            Q8=sQuery(id+"F2.wireOp",VERTEX,"E341");
            var Q9;
            Q9=sQuery(id+"F2.wireOp",VERTEX,"E342");
            var Q10;
            Q10=sQuery(id+"F2.wireOp",VERTEX,"E343");
            var Q11;
            Q11=sQuery(id+"F2.wireOp",VERTEX,"E344");
            var Q12;
            Q12=sQuery(id+"F2.wireOp",VERTEX,"E345");
            var Q13;
            Q13=sQuery(id+"F2.wireOp",VERTEX,"E346");
            var Q14;
            Q14=sQuery(id+"F2.wireOp",VERTEX,"E347");
            var Q15;
            Q15=sQuery(id+"F2.wireOp",VERTEX,"E348");
            var Q16;
            Q16=sQuery(id+"F2.wireOp",VERTEX,"E349");
            var Q17;
            Q17=sQuery(id+"F2.wireOp",VERTEX,"E350");
            var Q18;
            Q18=sQuery(id+"F2.wireOp",VERTEX,"E359");
            var Q19;
            Q19=sQuery(id+"F2.wireOp",VERTEX,"E360");
            var Q20;
            Q20=sQuery(id+"F2.wireOp",VERTEX,"E650.center");
            var Q21;
            Q21=sQuery(id+"F2.wireOp",VERTEX,"E362");
            var Q22;
            Q22=sQuery(id+"F2.wireOp",VERTEX,"E363");
            var Q23;
            Q23=sQuery(id+"F2.wireOp",VERTEX,"E364");
            var Q24;
            Q24=sQuery(id+"F2.wireOp",VERTEX,"E365");
            var Q25;
            Q25=sQuery(id+"F2.wireOp",VERTEX,"E366");
            var Q26;
            Q26=sQuery(id+"F2.wireOp",VERTEX,"E656.center");
            var Q27;
            Q27=sQuery(id+"F2.wireOp",VERTEX,"E368");
            var Q28;
            Q28=sQuery(id+"F2.wireOp",VERTEX,"E658.center");
            var Q29;
            Q29=sQuery(id+"F2.wireOp",VERTEX,"E659.center");
            var Q30;
            Q30=sQuery(id+"F2.wireOp",VERTEX,"E356");
            var Q31;
            Q31=sQuery(id+"F2.wireOp",VERTEX,"E355");
            var Q32;
            Q32=sQuery(id+"F2.wireOp",VERTEX,"E354");
            var Q33;
            Q33=sQuery(id+"F2.wireOp",VERTEX,"E353");
            var Q34;
            Q34=sQuery(id+"F2.wireOp",VERTEX,"E352");
            var Q35;
            Q35=sQuery(id+"F2.wireOp",VERTEX,"E351");
            var Q36;
            Q36=makeQuery(id+"F1.opExtrude","SWEPT_BODY",BODY,{"disambiguationData":[OSD([sQuery(id+"F0.wireOp",EDGE,"E0.bottom"),sQuery(id+"F0.wireOp",EDGE,"E0.top"),sQuery(id+"F0.wireOp",EDGE,"E0.left"),sQuery(id+"F0.wireOp",EDGE,"E0.right")])]});
            hole(context, id + "F7", {"style" : HoleStyle.SIMPLE, "endStyle" : HoleEndStyle.THROUGH, "holeDiameter" : 16 * mm, "majorDiameter" : 6.35 * mm, "isTappedThrough" : true, "tappedDepth" : 12.7 * mm, "tapClearance" : 3, "locations" : qUnion([Q0, Q1, Q2, Q3, Q4, Q5, Q6, Q7, Q8, Q9, Q10, Q11, Q12, Q13, Q14, Q15, Q16, Q17, Q18, Q19, Q20, Q21, Q22, Q23, Q24, Q25, Q26, Q27, Q28, Q29, Q30, Q31, Q32, Q33, Q34, Q35]), "scope" : qUnion([Q36])});
        }
        {
            var Q0;
            Q0=makeQuery(id+"F1.opExtrude","SWEPT_FACE",FACE,{"disambiguationData":[OSD([sQuery(id+"F0.wireOp",EDGE,"E0.left")])]});
            var sketch = newSketch(context, id + "F8", { "sketchPlane" : qUnion([Q0])});
            skLineSegment(sketch, "E682.bottom", {"start": v(-457.2, 0) * mm, "end": v(457.2, 0) * mm});
            skLineSegment(sketch, "E682.top", {"start": v(-457.2, -146.05) * mm, "end": v(457.2, -146.05) * mm});
            skLineSegment(sketch, "E682.left", {"start": v(-457.2, 0) * mm, "end": v(-457.2, -146.05) * mm});
            skLineSegment(sketch, "E682.right", {"start": v(457.2, 0) * mm, "end": v(457.2, -146.05) * mm});
            skSolve(sketch);
        }
        {
            var Q0;
            Q0=makeQuery(id+"F8.imprint","IMPRINT",FACE,{"disambiguationData":[TD([[makeQuery(id+"F8.imprint","IMPRINT",EDGE,{"derivedFrom":sQuery(id+"F8.wireOp",EDGE,"E682.bottom")}),-1.0]])]});
            extrude(context, id + "F9", {"entities" : qUnion([Q0]), "oppositeDirection" : true, "depth" : 6.35 * mm, "offsetDistance" : 25.4 * mm});
        }
        {
            var Q0;
            Q0=makeQuery(id+"F1.opExtrude","SWEPT_FACE",FACE,{"disambiguationData":[OSD([sQuery(id+"F0.wireOp",EDGE,"E0.top")])]});
            var sketch = newSketch(context, id + "F10", { "sketchPlane" : qUnion([Q0])});
            skLineSegment(sketch, "E683.bottom", {"start": v(-457.2, 0) * mm, "end": v(457.2, 0) * mm});
            skLineSegment(sketch, "E683.top", {"start": v(-457.2, -146.05) * mm, "end": v(457.2, -146.05) * mm});
            skLineSegment(sketch, "E683.left", {"start": v(-457.2, 0) * mm, "end": v(-457.2, -146.05) * mm});
            skLineSegment(sketch, "E683.right", {"start": v(457.2, 0) * mm, "end": v(457.2, -146.05) * mm});
            skSolve(sketch);
        }
        {
            var Q0;
            Q0=makeQuery(id+"F10.imprint","IMPRINT",FACE,{"disambiguationData":[TD([[makeQuery(id+"F10.imprint","IMPRINT",EDGE,{"derivedFrom":sQuery(id+"F10.wireOp",EDGE,"E683.bottom")}),-1.0]])]});
            extrude(context, id + "F11", {"entities" : qUnion([Q0]), "operationType" : NewBodyOperationType.ADD, "oppositeDirection" : true, "depth" : 6.35 * mm, "offsetDistance" : 25.4 * mm});
        }
        {
            var Q0;
            Q0=makeQuery(id+"F1.opExtrude","SWEPT_FACE",FACE,{"disambiguationData":[OSD([sQuery(id+"F0.wireOp",EDGE,"E0.right")])]});
            var sketch = newSketch(context, id + "F12", { "sketchPlane" : qUnion([Q0])});
            skLineSegment(sketch, "E684.bottom", {"start": v(-457.2, 0) * mm, "end": v(457.2, 0) * mm});
            skLineSegment(sketch, "E684.top", {"start": v(-457.2, -146.05) * mm, "end": v(457.2, -146.05) * mm});
            skLineSegment(sketch, "E684.left", {"start": v(-457.2, 0) * mm, "end": v(-457.2, -146.05) * mm});
            skLineSegment(sketch, "E684.right", {"start": v(457.2, 0) * mm, "end": v(457.2, -146.05) * mm});
            skSolve(sketch);
        }
        {
            var Q0;
            Q0=makeQuery(id+"F12.imprint","IMPRINT",FACE,{"disambiguationData":[TD([[makeQuery(id+"F12.imprint","IMPRINT",EDGE,{"derivedFrom":sQuery(id+"F12.wireOp",EDGE,"E684.bottom")}),1.0]])]});
            extrude(context, id + "F13", {"entities" : qUnion([Q0]), "oppositeDirection" : true, "depth" : 6.35 * mm, "offsetDistance" : 25.4 * mm});
        }
        {
            var Q0;
            Q0=makeQuery(id+"F1.opExtrude","SWEPT_FACE",FACE,{"disambiguationData":[OSD([sQuery(id+"F0.wireOp",EDGE,"E0.bottom")])]});
            var sketch = newSketch(context, id + "F14", { "sketchPlane" : qUnion([Q0])});
            skLineSegment(sketch, "E685.bottom", {"start": v(-457.2, 0) * mm, "end": v(457.2, 0) * mm});
            skLineSegment(sketch, "E685.top", {"start": v(-457.2, -146.05) * mm, "end": v(457.2, -146.05) * mm});
            skLineSegment(sketch, "E685.left", {"start": v(-457.2, 0) * mm, "end": v(-457.2, -146.05) * mm});
            skLineSegment(sketch, "E685.right", {"start": v(457.2, 0) * mm, "end": v(457.2, -146.05) * mm});
            skSolve(sketch);
        }
        {
            var Q0;
            Q0=makeQuery(id+"F14.imprint","IMPRINT",FACE,{"disambiguationData":[TD([[makeQuery(id+"F14.imprint","IMPRINT",EDGE,{"derivedFrom":sQuery(id+"F14.wireOp",EDGE,"E685.bottom")}),1.0]])]});
            extrude(context, id + "F15", {"entities" : qUnion([Q0]), "oppositeDirection" : true, "depth" : 6.35 * mm, "offsetDistance" : 25.4 * mm});
        }
        {
            var Q0;
            Q0=makeQuery(id+"F9.opExtrude","CAP_FACE",FACE,{"disambiguationData":[OSD([sQuery(id+"F8.wireOp",EDGE,"E682.bottom"),sQuery(id+"F8.wireOp",EDGE,"E682.top"),sQuery(id+"F8.wireOp",EDGE,"E682.left"),sQuery(id+"F8.wireOp",EDGE,"E682.right")])],"isStart":true});
            var sketch = newSketch(context, id + "F16", { "sketchPlane" : qUnion([Q0])});
            skLineSegment(sketch, "E686", {"start": v(-457.2, -19.05) * mm, "end": v(457.2, -19.05) * mm, "construction": true});
            skLineSegment(sketch, "E687", {"start": v(-457.2, -73.03) * mm, "end": v(457.2, -73.03) * mm, "construction": true});
            skLineSegment(sketch, "E688", {"start": v(-457.2, -123.83) * mm, "end": v(457.2, -123.83) * mm, "construction": true});
            skLineSegment(sketch, "E689", {"start": v(431.8, 0) * mm, "end": v(431.8, -146.05) * mm, "construction": true});
            skLineSegment(sketch, "E690", {"start": v(381, 0) * mm, "end": v(381, -146.05) * mm, "construction": true});
            skLineSegment(sketch, "E691", {"start": v(330.2, 0) * mm, "end": v(330.2, -146.05) * mm, "construction": true});
            skLineSegment(sketch, "E692", {"start": v(279.4, 0) * mm, "end": v(279.4, -146.05) * mm, "construction": true});
            skLineSegment(sketch, "E693", {"start": v(228.6, 0) * mm, "end": v(228.6, -146.05) * mm, "construction": true});
            skLineSegment(sketch, "E694", {"start": v(177.8, 0) * mm, "end": v(177.8, -146.05) * mm, "construction": true});
            skLineSegment(sketch, "E695", {"start": v(127, 0) * mm, "end": v(127, -146.05) * mm, "construction": true});
            skLineSegment(sketch, "E696", {"start": v(76.2, 0) * mm, "end": v(76.2, -146.05) * mm, "construction": true});
            skLineSegment(sketch, "E697", {"start": v(25.4, 0) * mm, "end": v(25.4, -146.05) * mm, "construction": true});
            skLineSegment(sketch, "E698", {"start": v(-25.4, 0) * mm, "end": v(-25.4, -146.05) * mm, "construction": true});
            skLineSegment(sketch, "E699", {"start": v(-76.2, 0) * mm, "end": v(-76.2, -146.05) * mm, "construction": true});
            skLineSegment(sketch, "E700", {"start": v(-127, 0) * mm, "end": v(-127, -146.05) * mm, "construction": true});
            skLineSegment(sketch, "E701", {"start": v(-177.8, 0) * mm, "end": v(-177.8, -146.05) * mm, "construction": true});
            skLineSegment(sketch, "E702", {"start": v(-228.6, 0) * mm, "end": v(-228.6, -146.05) * mm, "construction": true});
            skLineSegment(sketch, "E703", {"start": v(-279.4, 0) * mm, "end": v(-279.4, -146.05) * mm, "construction": true});
            skLineSegment(sketch, "E704", {"start": v(-330.2, 0) * mm, "end": v(-330.2, -146.05) * mm, "construction": true});
            skLineSegment(sketch, "E705", {"start": v(-381, 0) * mm, "end": v(-381, -146.05) * mm, "construction": true});
            skLineSegment(sketch, "E706", {"start": v(-431.8, 0) * mm, "end": v(-431.8, -146.05) * mm, "construction": true});
            skPoint(sketch, "E707", {"position": v(-431.8, -19.05) * mm});
            skPoint(sketch, "E708", {"position": v(-381, -19.05) * mm});
            skPoint(sketch, "E709", {"position": v(-330.2, -19.05) * mm});
            skPoint(sketch, "E710", {"position": v(-279.4, -19.05) * mm});
            skPoint(sketch, "E711", {"position": v(-228.6, -19.05) * mm});
            skPoint(sketch, "E712", {"position": v(-177.8, -19.05) * mm});
            skPoint(sketch, "E713", {"position": v(-127, -19.05) * mm});
            skPoint(sketch, "E714", {"position": v(-76.2, -19.05) * mm});
            skPoint(sketch, "E715", {"position": v(-25.4, -19.05) * mm});
            skPoint(sketch, "E716", {"position": v(25.4, -19.05) * mm});
            skPoint(sketch, "E717", {"position": v(76.2, -19.05) * mm});
            skPoint(sketch, "E718", {"position": v(127, -19.05) * mm});
            skPoint(sketch, "E719", {"position": v(177.8, -19.05) * mm});
            skPoint(sketch, "E720", {"position": v(228.6, -19.05) * mm});
            skPoint(sketch, "E721", {"position": v(279.4, -19.05) * mm});
            skPoint(sketch, "E722", {"position": v(330.2, -19.05) * mm});
            skPoint(sketch, "E723", {"position": v(381, -19.05) * mm});
            skPoint(sketch, "E724", {"position": v(431.8, -19.05) * mm});
            skPoint(sketch, "E725", {"position": v(-431.8, -73.03) * mm});
            skPoint(sketch, "E726", {"position": v(-431.8, -123.83) * mm});
            skPoint(sketch, "E727", {"position": v(-381, -73.03) * mm});
            skPoint(sketch, "E728", {"position": v(-330.2, -73.03) * mm});
            skPoint(sketch, "E729", {"position": v(-279.4, -73.03) * mm});
            skPoint(sketch, "E730", {"position": v(-228.6, -73.03) * mm});
            skPoint(sketch, "E731", {"position": v(-177.8, -73.03) * mm});
            skPoint(sketch, "E732", {"position": v(-127, -73.03) * mm});
            skPoint(sketch, "E733", {"position": v(-76.2, -73.03) * mm});
            skPoint(sketch, "E734", {"position": v(-25.4, -73.03) * mm});
            skPoint(sketch, "E735", {"position": v(25.4, -73.03) * mm});
            skPoint(sketch, "E736", {"position": v(76.2, -73.03) * mm});
            skPoint(sketch, "E737", {"position": v(127, -73.03) * mm});
            skPoint(sketch, "E738", {"position": v(177.8, -73.03) * mm});
            skPoint(sketch, "E739", {"position": v(228.6, -73.03) * mm});
            skPoint(sketch, "E740", {"position": v(279.4, -73.03) * mm});
            skPoint(sketch, "E741", {"position": v(330.2, -73.03) * mm});
            skPoint(sketch, "E742", {"position": v(381, -73.03) * mm});
            skPoint(sketch, "E743", {"position": v(431.8, -73.03) * mm});
            skPoint(sketch, "E744", {"position": v(431.8, -123.83) * mm});
            skPoint(sketch, "E745", {"position": v(381, -123.83) * mm});
            skPoint(sketch, "E746", {"position": v(330.2, -123.83) * mm});
            skPoint(sketch, "E747", {"position": v(279.4, -123.83) * mm});
            skPoint(sketch, "E748", {"position": v(228.6, -123.83) * mm});
            skPoint(sketch, "E749", {"position": v(177.8, -123.83) * mm});
            skPoint(sketch, "E750", {"position": v(127, -123.83) * mm});
            skPoint(sketch, "E751", {"position": v(76.2, -123.83) * mm});
            skPoint(sketch, "E752", {"position": v(25.4, -123.83) * mm});
            skPoint(sketch, "E753", {"position": v(-25.4, -123.83) * mm});
            skPoint(sketch, "E754", {"position": v(-76.2, -123.83) * mm});
            skPoint(sketch, "E755", {"position": v(-127, -123.83) * mm});
            skPoint(sketch, "E756", {"position": v(-177.8, -123.83) * mm});
            skPoint(sketch, "E757", {"position": v(-228.6, -123.83) * mm});
            skPoint(sketch, "E758", {"position": v(-279.4, -123.83) * mm});
            skPoint(sketch, "E759", {"position": v(-330.2, -123.83) * mm});
            skPoint(sketch, "E760", {"position": v(-381, -123.83) * mm});
            skSolve(sketch);
        }
        {
            var Q0;
            Q0=makeQuery(id+"F13.opExtrude","CAP_FACE",FACE,{"disambiguationData":[OSD([sQuery(id+"F12.wireOp",EDGE,"E684.bottom"),sQuery(id+"F12.wireOp",EDGE,"E684.top"),sQuery(id+"F12.wireOp",EDGE,"E684.left"),sQuery(id+"F12.wireOp",EDGE,"E684.right")])],"isStart":true});
            var sketch = newSketch(context, id + "F17", { "sketchPlane" : qUnion([Q0])});
            skLineSegment(sketch, "E761", {"start": v(-457.2, -19.05) * mm, "end": v(457.2, -19.05) * mm, "construction": true});
            skLineSegment(sketch, "E762", {"start": v(-457.2, -73.02) * mm, "end": v(457.2, -73.02) * mm, "construction": true});
            skLineSegment(sketch, "E763", {"start": v(-457.2, -123.82) * mm, "end": v(457.2, -123.82) * mm, "construction": true});
            skSolve(sketch);
        }
        {
            var Q0;
            Q0=sQuery(id+"F16.wireOp",VERTEX,"E707");
            var Q1;
            Q1=sQuery(id+"F16.wireOp",VERTEX,"E708");
            var Q2;
            Q2=sQuery(id+"F16.wireOp",VERTEX,"E709");
            var Q3;
            Q3=sQuery(id+"F16.wireOp",VERTEX,"E710");
            var Q4;
            Q4=sQuery(id+"F16.wireOp",VERTEX,"E711");
            var Q5;
            Q5=sQuery(id+"F16.wireOp",VERTEX,"E712");
            var Q6;
            Q6=sQuery(id+"F16.wireOp",VERTEX,"E713");
            var Q7;
            Q7=sQuery(id+"F16.wireOp",VERTEX,"E714");
            var Q8;
            Q8=sQuery(id+"F16.wireOp",VERTEX,"E715");
            var Q9;
            Q9=sQuery(id+"F16.wireOp",VERTEX,"E716");
            var Q10;
            Q10=sQuery(id+"F16.wireOp",VERTEX,"E717");
            var Q11;
            Q11=sQuery(id+"F16.wireOp",VERTEX,"E718");
            var Q12;
            Q12=sQuery(id+"F16.wireOp",VERTEX,"E719");
            var Q13;
            Q13=sQuery(id+"F16.wireOp",VERTEX,"E720");
            var Q14;
            Q14=sQuery(id+"F16.wireOp",VERTEX,"E721");
            var Q15;
            Q15=sQuery(id+"F16.wireOp",VERTEX,"E722");
            var Q16;
            Q16=sQuery(id+"F16.wireOp",VERTEX,"E723");
            var Q17;
            Q17=sQuery(id+"F16.wireOp",VERTEX,"E724");
            var Q18;
            Q18=sQuery(id+"F16.wireOp",VERTEX,"E725");
            var Q19;
            Q19=sQuery(id+"F16.wireOp",VERTEX,"E727");
            var Q20;
            Q20=sQuery(id+"F16.wireOp",VERTEX,"E728");
            var Q21;
            Q21=sQuery(id+"F16.wireOp",VERTEX,"E729");
            var Q22;
            Q22=sQuery(id+"F16.wireOp",VERTEX,"E730");
            var Q23;
            Q23=sQuery(id+"F16.wireOp",VERTEX,"E731");
            var Q24;
            Q24=sQuery(id+"F16.wireOp",VERTEX,"E732");
            var Q25;
            Q25=sQuery(id+"F16.wireOp",VERTEX,"E733");
            var Q26;
            Q26=sQuery(id+"F16.wireOp",VERTEX,"E734");
            var Q27;
            Q27=sQuery(id+"F16.wireOp",VERTEX,"E735");
            var Q28;
            Q28=sQuery(id+"F16.wireOp",VERTEX,"E736");
            var Q29;
            Q29=sQuery(id+"F16.wireOp",VERTEX,"E737");
            var Q30;
            Q30=sQuery(id+"F16.wireOp",VERTEX,"E738");
            var Q31;
            Q31=sQuery(id+"F16.wireOp",VERTEX,"E739");
            var Q32;
            Q32=sQuery(id+"F16.wireOp",VERTEX,"E740");
            var Q33;
            Q33=sQuery(id+"F16.wireOp",VERTEX,"E741");
            var Q34;
            Q34=sQuery(id+"F16.wireOp",VERTEX,"E742");
            var Q35;
            Q35=sQuery(id+"F16.wireOp",VERTEX,"E743");
            var Q36;
            Q36=sQuery(id+"F16.wireOp",VERTEX,"E726");
            var Q37;
            Q37=sQuery(id+"F16.wireOp",VERTEX,"E760");
            var Q38;
            Q38=sQuery(id+"F16.wireOp",VERTEX,"E759");
            var Q39;
            Q39=sQuery(id+"F16.wireOp",VERTEX,"E758");
            var Q40;
            Q40=sQuery(id+"F16.wireOp",VERTEX,"E757");
            var Q41;
            Q41=sQuery(id+"F16.wireOp",VERTEX,"E756");
            var Q42;
            Q42=sQuery(id+"F16.wireOp",VERTEX,"E755");
            var Q43;
            Q43=sQuery(id+"F16.wireOp",VERTEX,"E754");
            var Q44;
            Q44=sQuery(id+"F16.wireOp",VERTEX,"E753");
            var Q45;
            Q45=sQuery(id+"F16.wireOp",VERTEX,"E752");
            var Q46;
            Q46=sQuery(id+"F16.wireOp",VERTEX,"E751");
            var Q47;
            Q47=sQuery(id+"F16.wireOp",VERTEX,"E750");
            var Q48;
            Q48=sQuery(id+"F16.wireOp",VERTEX,"E749");
            var Q49;
            Q49=sQuery(id+"F16.wireOp",VERTEX,"E748");
            var Q50;
            Q50=sQuery(id+"F16.wireOp",VERTEX,"E747");
            var Q51;
            Q51=sQuery(id+"F16.wireOp",VERTEX,"E746");
            var Q52;
            Q52=sQuery(id+"F16.wireOp",VERTEX,"E745");
            var Q53;
            Q53=sQuery(id+"F16.wireOp",VERTEX,"E744");
            var Q54;
            Q54=makeQuery(id+"F9.opExtrude","SWEPT_BODY",BODY,{"disambiguationData":[OSD([sQuery(id+"F8.wireOp",EDGE,"E682.bottom"),sQuery(id+"F8.wireOp",EDGE,"E682.top"),sQuery(id+"F8.wireOp",EDGE,"E682.left"),sQuery(id+"F8.wireOp",EDGE,"E682.right")])]});
            var Q55;
            Q55=makeQuery(id+"F13.opExtrude","SWEPT_BODY",BODY,{"disambiguationData":[OSD([sQuery(id+"F12.wireOp",EDGE,"E684.bottom"),sQuery(id+"F12.wireOp",EDGE,"E684.top"),sQuery(id+"F12.wireOp",EDGE,"E684.left"),sQuery(id+"F12.wireOp",EDGE,"E684.right")])]});
            hole(context, id + "F18", {"style" : HoleStyle.SIMPLE, "endStyle" : HoleEndStyle.THROUGH, "holeDiameter" : 16 * mm, "majorDiameter" : 6.35 * mm, "isTappedThrough" : true, "tappedDepth" : 12.7 * mm, "tapClearance" : 3, "locations" : qUnion([Q0, Q1, Q2, Q3, Q4, Q5, Q6, Q7, Q8, Q9, Q10, Q11, Q12, Q13, Q14, Q15, Q16, Q17, Q18, Q19, Q20, Q21, Q22, Q23, Q24, Q25, Q26, Q27, Q28, Q29, Q30, Q31, Q32, Q33, Q34, Q35, Q36, Q37, Q38, Q39, Q40, Q41, Q42, Q43, Q44, Q45, Q46, Q47, Q48, Q49, Q50, Q51, Q52, Q53]), "scope" : qUnion([Q54, Q55])});
        }
        {
            var Q0;
            Q0=makeQuery(id+"F10.imprint","IMPRINT",FACE,{"disambiguationData":[TD([[makeQuery(id+"F10.imprint","IMPRINT",EDGE,{"derivedFrom":sQuery(id+"F10.wireOp",EDGE,"E683.bottom")}),-1.0]])]});
            var sketch = newSketch(context, id + "F19", { "sketchPlane" : qUnion([Q0])});
            skLineSegment(sketch, "E764", {"start": v(-463.08, -19.05) * mm, "end": v(461, -19.05) * mm, "construction": true});
            skLineSegment(sketch, "E765", {"start": v(-463.08, -69.85) * mm, "end": v(462.1, -69.85) * mm, "construction": true});
            skLineSegment(sketch, "E766", {"start": v(-461.98, -120.65) * mm, "end": v(459.9, -120.65) * mm, "construction": true});
            skLineSegment(sketch, "E767", {"start": v(-431.8, 9.69) * mm, "end": v(-431.8, -144.88) * mm, "construction": true});
            skLineSegment(sketch, "E768", {"start": v(-381, 10.8) * mm, "end": v(-381, -148.19) * mm, "construction": true});
            skLineSegment(sketch, "E769", {"start": v(-330.2, 9.69) * mm, "end": v(-330.2, -145.98) * mm, "construction": true});
            skLineSegment(sketch, "E770", {"start": v(-279.4, 9.69) * mm, "end": v(-279.4, -145.98) * mm, "construction": true});
            skLineSegment(sketch, "E771", {"start": v(-228.6, 0) * mm, "end": v(-228.6, -150.4) * mm, "construction": true});
            skLineSegment(sketch, "E772", {"start": v(-177.8, 0) * mm, "end": v(-177.8, -147.08) * mm, "construction": true});
            skLineSegment(sketch, "E773", {"start": v(-127, 0) * mm, "end": v(-127, -149.3) * mm, "construction": true});
            skLineSegment(sketch, "E774", {"start": v(-76.2, 0) * mm, "end": v(-76.2, -149.3) * mm, "construction": true});
            skLineSegment(sketch, "E775", {"start": v(-25.4, 0) * mm, "end": v(-25.4, -148.19) * mm, "construction": true});
            skLineSegment(sketch, "E776", {"start": v(25.4, 9.69) * mm, "end": v(25.4, -150.4) * mm, "construction": true});
            skLineSegment(sketch, "E777", {"start": v(76.2, 0) * mm, "end": v(76.2, -150.4) * mm, "construction": true});
            skLineSegment(sketch, "E778", {"start": v(127, 0) * mm, "end": v(127, -151.5) * mm, "construction": true});
            skLineSegment(sketch, "E779", {"start": v(177.8, 9.69) * mm, "end": v(177.8, -150.4) * mm, "construction": true});
            skLineSegment(sketch, "E780", {"start": v(228.6, 0) * mm, "end": v(228.6, -147.08) * mm, "construction": true});
            skLineSegment(sketch, "E781", {"start": v(279.4, 0) * mm, "end": v(279.4, -143.77) * mm, "construction": true});
            skLineSegment(sketch, "E782", {"start": v(330.2, 9.69) * mm, "end": v(330.2, -147.08) * mm, "construction": true});
            skLineSegment(sketch, "E783", {"start": v(381, 0) * mm, "end": v(381, -147.08) * mm, "construction": true});
            skLineSegment(sketch, "E784", {"start": v(431.8, 0) * mm, "end": v(431.8, -147.08) * mm, "construction": true});
            skPoint(sketch, "E785", {"position": v(-431.8, -19.05) * mm});
            skPoint(sketch, "E786", {"position": v(-381, -19.05) * mm});
            skPoint(sketch, "E787", {"position": v(-330.2, -19.05) * mm});
            skPoint(sketch, "E788", {"position": v(-279.4, -19.05) * mm});
            skPoint(sketch, "E789", {"position": v(-228.6, -19.05) * mm});
            skPoint(sketch, "E790", {"position": v(-177.8, -19.05) * mm});
            skPoint(sketch, "E791", {"position": v(-127, -19.05) * mm});
            skPoint(sketch, "E792", {"position": v(-76.2, -19.05) * mm});
            skPoint(sketch, "E793", {"position": v(-25.4, -19.05) * mm});
            skPoint(sketch, "E794", {"position": v(25.4, -19.05) * mm});
            skPoint(sketch, "E795", {"position": v(76.2, -19.05) * mm});
            skPoint(sketch, "E796", {"position": v(127, -19.05) * mm});
            skPoint(sketch, "E797", {"position": v(177.8, -19.05) * mm});
            skPoint(sketch, "E798", {"position": v(228.6, -19.05) * mm});
            skPoint(sketch, "E799", {"position": v(279.4, -19.05) * mm});
            skPoint(sketch, "E800", {"position": v(330.2, -19.05) * mm});
            skPoint(sketch, "E801", {"position": v(381, -19.05) * mm});
            skPoint(sketch, "E802", {"position": v(431.8, -19.05) * mm});
            skPoint(sketch, "E803", {"position": v(-431.8, -69.85) * mm});
            skPoint(sketch, "E804", {"position": v(-381, -68.7) * mm});
            skPoint(sketch, "E805", {"position": v(-330.2, -69.85) * mm});
            skPoint(sketch, "E806", {"position": v(-279.4, -69.85) * mm});
            skPoint(sketch, "E807", {"position": v(-228.6, -69.85) * mm});
            skPoint(sketch, "E808", {"position": v(-177.8, -69.85) * mm});
            skPoint(sketch, "E809", {"position": v(-127, -69.85) * mm});
            skPoint(sketch, "E810", {"position": v(-76.2, -69.85) * mm});
            skPoint(sketch, "E811", {"position": v(-25.4, -69.85) * mm});
            skPoint(sketch, "E812", {"position": v(25.4, -69.85) * mm});
            skPoint(sketch, "E813", {"position": v(76.2, -69.85) * mm});
            skPoint(sketch, "E814", {"position": v(127, -69.85) * mm});
            skPoint(sketch, "E815", {"position": v(177.8, -69.85) * mm});
            skPoint(sketch, "E816", {"position": v(228.6, -69.85) * mm});
            skPoint(sketch, "E817", {"position": v(279.4, -69.85) * mm});
            skPoint(sketch, "E818", {"position": v(330.2, -69.85) * mm});
            skPoint(sketch, "E819", {"position": v(381, -69.85) * mm});
            skPoint(sketch, "E820", {"position": v(431.8, -69.85) * mm});
            skPoint(sketch, "E821", {"position": v(431.8, -120.65) * mm});
            skPoint(sketch, "E822", {"position": v(381, -120.65) * mm});
            skPoint(sketch, "E823", {"position": v(330.2, -120.65) * mm});
            skPoint(sketch, "E824", {"position": v(279.4, -120.65) * mm});
            skPoint(sketch, "E825", {"position": v(228.6, -120.65) * mm});
            skPoint(sketch, "E826", {"position": v(177.8, -120.65) * mm});
            skPoint(sketch, "E827", {"position": v(127, -120.65) * mm});
            skPoint(sketch, "E828", {"position": v(76.2, -120.65) * mm});
            skPoint(sketch, "E829", {"position": v(25.4, -120.65) * mm});
            skPoint(sketch, "E830", {"position": v(-25.4, -120.65) * mm});
            skPoint(sketch, "E831", {"position": v(-76.2, -120.65) * mm});
            skPoint(sketch, "E832", {"position": v(-127, -120.65) * mm});
            skPoint(sketch, "E833", {"position": v(-177.8, -120.65) * mm});
            skPoint(sketch, "E834", {"position": v(-228.6, -120.65) * mm});
            skPoint(sketch, "E835", {"position": v(-279.4, -120.65) * mm});
            skPoint(sketch, "E836", {"position": v(-330.2, -120.65) * mm});
            skPoint(sketch, "E837", {"position": v(-381, -120.65) * mm});
            skPoint(sketch, "E838", {"position": v(-431.8, -120.65) * mm});
            skSolve(sketch);
        }
        {
            var Q0;
            Q0=sQuery(id+"F19.wireOp",VERTEX,"E785");
            var Q1;
            Q1=sQuery(id+"F19.wireOp",VERTEX,"E786");
            var Q2;
            Q2=sQuery(id+"F19.wireOp",VERTEX,"E787");
            var Q3;
            Q3=sQuery(id+"F19.wireOp",VERTEX,"E788");
            var Q4;
            Q4=sQuery(id+"F19.wireOp",VERTEX,"E789");
            var Q5;
            Q5=sQuery(id+"F19.wireOp",VERTEX,"E790");
            var Q6;
            Q6=sQuery(id+"F19.wireOp",VERTEX,"E791");
            var Q7;
            Q7=sQuery(id+"F19.wireOp",VERTEX,"E792");
            var Q8;
            Q8=sQuery(id+"F19.wireOp",VERTEX,"E793");
            var Q9;
            Q9=sQuery(id+"F19.wireOp",VERTEX,"E794");
            var Q10;
            Q10=sQuery(id+"F19.wireOp",VERTEX,"E795");
            var Q11;
            Q11=sQuery(id+"F19.wireOp",VERTEX,"E796");
            var Q12;
            Q12=sQuery(id+"F19.wireOp",VERTEX,"E797");
            var Q13;
            Q13=sQuery(id+"F19.wireOp",VERTEX,"E798");
            var Q14;
            Q14=sQuery(id+"F19.wireOp",VERTEX,"E799");
            var Q15;
            Q15=sQuery(id+"F19.wireOp",VERTEX,"E800");
            var Q16;
            Q16=sQuery(id+"F19.wireOp",VERTEX,"E801");
            var Q17;
            Q17=sQuery(id+"F19.wireOp",VERTEX,"E802");
            var Q18;
            Q18=sQuery(id+"F19.wireOp",VERTEX,"E803");
            var Q19;
            Q19=sQuery(id+"F19.wireOp",VERTEX,"E804");
            var Q20;
            Q20=sQuery(id+"F19.wireOp",VERTEX,"E805");
            var Q21;
            Q21=sQuery(id+"F19.wireOp",VERTEX,"E806");
            var Q22;
            Q22=sQuery(id+"F19.wireOp",VERTEX,"E807");
            var Q23;
            Q23=sQuery(id+"F19.wireOp",VERTEX,"E808");
            var Q24;
            Q24=sQuery(id+"F19.wireOp",VERTEX,"E809");
            var Q25;
            Q25=sQuery(id+"F19.wireOp",VERTEX,"E810");
            var Q26;
            Q26=sQuery(id+"F19.wireOp",VERTEX,"E811");
            var Q27;
            Q27=sQuery(id+"F19.wireOp",VERTEX,"E812");
            var Q28;
            Q28=sQuery(id+"F19.wireOp",VERTEX,"E813");
            var Q29;
            Q29=sQuery(id+"F19.wireOp",VERTEX,"E814");
            var Q30;
            Q30=sQuery(id+"F19.wireOp",VERTEX,"E815");
            var Q31;
            Q31=sQuery(id+"F19.wireOp",VERTEX,"E816");
            var Q32;
            Q32=sQuery(id+"F19.wireOp",VERTEX,"E817");
            var Q33;
            Q33=sQuery(id+"F19.wireOp",VERTEX,"E818");
            var Q34;
            Q34=sQuery(id+"F19.wireOp",VERTEX,"E819");
            var Q35;
            Q35=sQuery(id+"F19.wireOp",VERTEX,"E820");
            var Q36;
            Q36=sQuery(id+"F19.wireOp",VERTEX,"E821");
            var Q37;
            Q37=sQuery(id+"F19.wireOp",VERTEX,"E822");
            var Q38;
            Q38=sQuery(id+"F19.wireOp",VERTEX,"E823");
            var Q39;
            Q39=sQuery(id+"F19.wireOp",VERTEX,"E824");
            var Q40;
            Q40=sQuery(id+"F19.wireOp",VERTEX,"E825");
            var Q41;
            Q41=sQuery(id+"F19.wireOp",VERTEX,"E826");
            var Q42;
            Q42=sQuery(id+"F19.wireOp",VERTEX,"E827");
            var Q43;
            Q43=sQuery(id+"F19.wireOp",VERTEX,"E828");
            var Q44;
            Q44=sQuery(id+"F19.wireOp",VERTEX,"E829");
            var Q45;
            Q45=sQuery(id+"F19.wireOp",VERTEX,"E830");
            var Q46;
            Q46=sQuery(id+"F19.wireOp",VERTEX,"E831");
            var Q47;
            Q47=sQuery(id+"F19.wireOp",VERTEX,"E832");
            var Q48;
            Q48=sQuery(id+"F19.wireOp",VERTEX,"E833");
            var Q49;
            Q49=sQuery(id+"F19.wireOp",VERTEX,"E834");
            var Q50;
            Q50=sQuery(id+"F19.wireOp",VERTEX,"E835");
            var Q51;
            Q51=sQuery(id+"F19.wireOp",VERTEX,"E836");
            var Q52;
            Q52=sQuery(id+"F19.wireOp",VERTEX,"E837");
            var Q53;
            Q53=sQuery(id+"F19.wireOp",VERTEX,"E838");
            var Q54;
            Q54=makeQuery(id+"F9.opExtrude","SWEPT_BODY",BODY,{"disambiguationData":[OSD([sQuery(id+"F8.wireOp",EDGE,"E682.bottom"),sQuery(id+"F8.wireOp",EDGE,"E682.top"),sQuery(id+"F8.wireOp",EDGE,"E682.left"),sQuery(id+"F8.wireOp",EDGE,"E682.right")])]});
            var Q55;
            Q55=makeQuery(id+"F15.opExtrude","SWEPT_BODY",BODY,{"disambiguationData":[OSD([sQuery(id+"F14.wireOp",EDGE,"E685.bottom"),sQuery(id+"F14.wireOp",EDGE,"E685.top"),sQuery(id+"F14.wireOp",EDGE,"E685.left"),sQuery(id+"F14.wireOp",EDGE,"E685.right")])]});
            hole(context, id + "F20", {"style" : HoleStyle.SIMPLE, "endStyle" : HoleEndStyle.THROUGH, "holeDiameter" : 16 * mm, "majorDiameter" : 6.35 * mm, "isTappedThrough" : true, "tappedDepth" : 12.7 * mm, "tapClearance" : 3, "locations" : qUnion([Q0, Q1, Q2, Q3, Q4, Q5, Q6, Q7, Q8, Q9, Q10, Q11, Q12, Q13, Q14, Q15, Q16, Q17, Q18, Q19, Q20, Q21, Q22, Q23, Q24, Q25, Q26, Q27, Q28, Q29, Q30, Q31, Q32, Q33, Q34, Q35, Q36, Q37, Q38, Q39, Q40, Q41, Q42, Q43, Q44, Q45, Q46, Q47, Q48, Q49, Q50, Q51, Q52, Q53]), "scope" : qUnion([Q54, Q55])});
        }
    });
